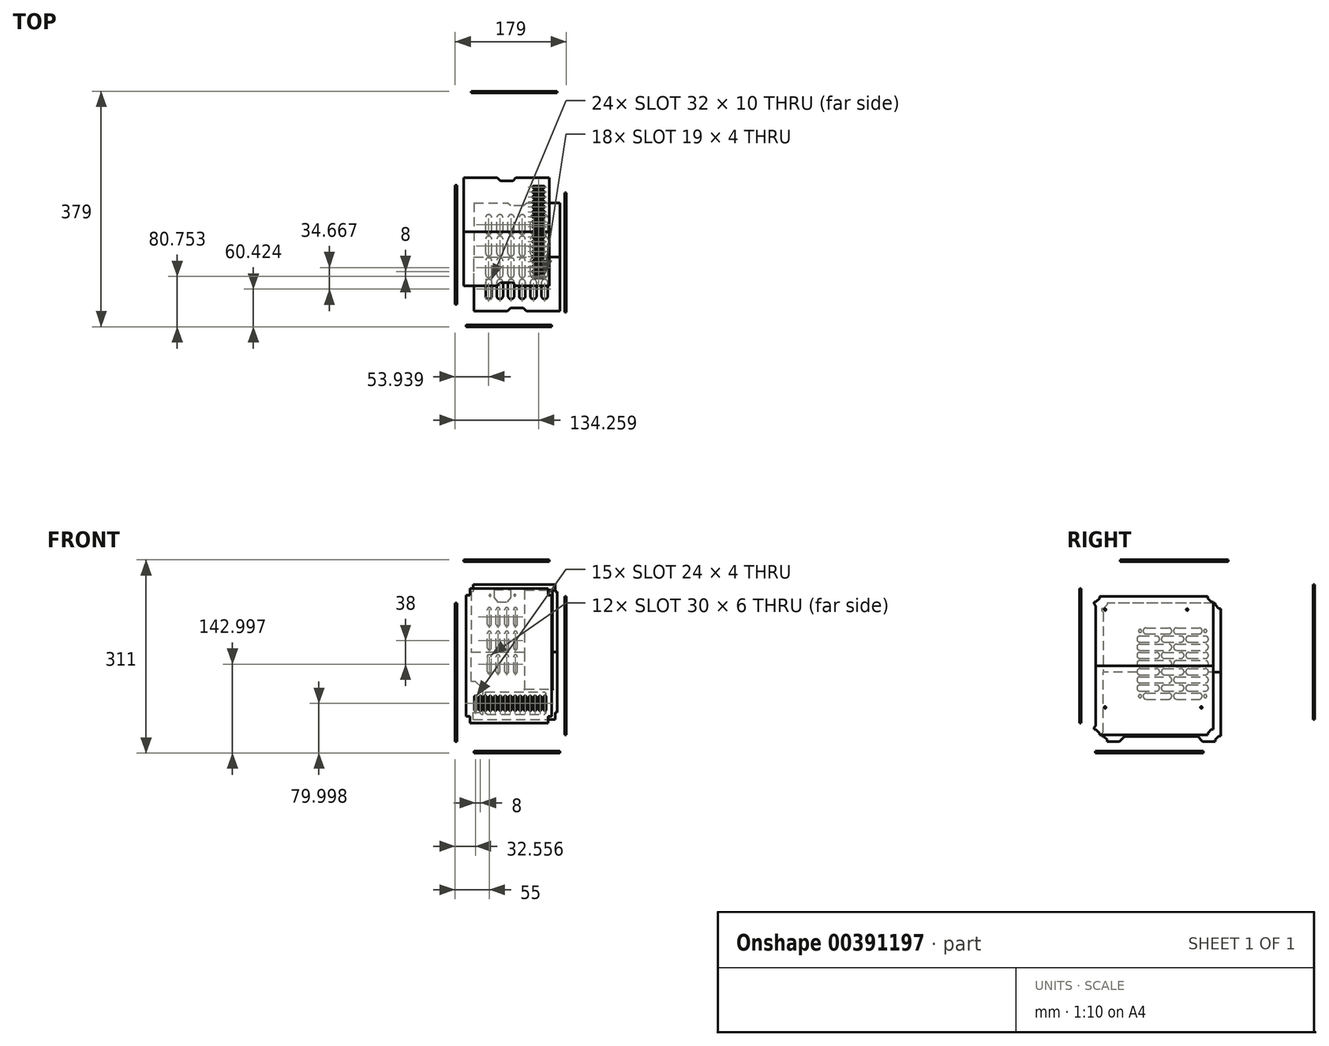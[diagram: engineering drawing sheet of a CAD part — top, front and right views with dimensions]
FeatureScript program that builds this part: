
annotation { "Feature Type Name" : "Feature", "Feature Type Description" : "" }
export const myFeature = defineFeature(function(context is Context, id is Id, definition is map)
    precondition{}
    {
        {
            var Q0;
            Q0=qCreatedBy(makeId("Front.planeOp"),FACE);
            var sketch = newSketch(context, id + "F0", { "sketchPlane" : qUnion([Q0])});
            skLineSegment(sketch, "E0.bottom", {"start": v(-78.44, 112) * mm, "end": v(59.56, 112) * mm});
            skLineSegment(sketch, "E0.top", {"start": v(-78.44, 3.5) * mm, "end": v(59.56, 3.5) * mm});
            skLineSegment(sketch, "E0.left", {"start": v(-78.44, 112) * mm, "end": v(-78.44, 3.5) * mm});
            skLineSegment(sketch, "E0.right", {"start": v(59.56, 112) * mm, "end": v(59.56, 3.5) * mm});
            skLineSegment(sketch, "E1", {"start": v(-78.44, 100.9) * mm, "end": v(-72.34, 100.9) * mm});
            skLineSegment(sketch, "E2", {"start": v(-72.34, 100.9) * mm, "end": v(-72.34, 112) * mm});
            skLineSegment(sketch, "E3", {"start": v(53.46, 112) * mm, "end": v(53.46, 100.9) * mm});
            skLineSegment(sketch, "E4", {"start": v(53.46, 100.9) * mm, "end": v(59.56, 100.9) * mm});
            skSolve(sketch);
        }
        {
            var Q0;
            {var subQ1=sQuery(id+"F0.wireOp",EDGE,"E0.top");Q0=makeQuery(id+"F0.imprint","IMPRINT",FACE,{"disambiguationData":[TD([[makeQuery(id+"F0.imprint","IMPRINT",EDGE,{"derivedFrom":subQ1}),1.0]])]});}
            extrude(context, id + "F1", {"entities" : qUnion([Q0]), "depth" : 3 * mm});
        }
        {
            var Q0;
            Q0=makeQuery(id+"F1.opExtrude","SWEPT_BODY",BODY,{"disambiguationData":[OSD([sQuery(id+"F0.wireOp",EDGE,"E0.bottom"),sQuery(id+"F0.wireOp",EDGE,"E0.top"),sQuery(id+"F0.wireOp",EDGE,"E0.left"),sQuery(id+"F0.wireOp",EDGE,"E0.right"),sQuery(id+"F0.wireOp",EDGE,"f4ycc0LQ-zHDD-6vh2-nqyr-j4wCRgx8H2At"),sQuery(id+"F0.wireOp",EDGE,"8WAKjnjZ-eP6i-UWzr-gM63-qz3cF0Hyub4H"),sQuery(id+"F0.wireOp",EDGE,"8kIEKiAh-QTEb-dtpp-JcTS-wpPMPQfBbqQd"),sQuery(id+"F0.wireOp",EDGE,"IAD0FTGy-GJaP-wMLm-guci-XfnhwucHu2uu"),sQuery(id+"F0.wireOp",EDGE,"IvHsRxJE-VIxi-RXbs-pRJC-tqeUj7lQNFDg"),sQuery(id+"F0.wireOp",EDGE,"jDx6nEBO-jJHg-Gf5S-wIms-nsZNRVFYcTxt")])]});
            var Q1;
            Q1=makeQuery(id+"F1.opExtrude","SWEPT_FACE",FACE,{"disambiguationData":[OSD([sQuery(id+"F0.wireOp",EDGE,"E0.top")])]});
            mirror(context, id + "F2", {"operationType" : NewBodyOperationType.ADD, "entities" : qUnion([Q0]), "mirrorPlane" : qUnion([Q1])});
        }
        {
            var Q0;
            {var subQ0=makeQuery(id+"F1.opExtrude","CAP_FACE",FACE,{"disambiguationData":[OSD([sQuery(id+"F0.wireOp",EDGE,"E0.bottom"),sQuery(id+"F0.wireOp",EDGE,"E0.top"),sQuery(id+"F0.wireOp",EDGE,"E0.left"),sQuery(id+"F0.wireOp",EDGE,"E0.right"),sQuery(id+"F0.wireOp",EDGE,"f4ycc0LQ-zHDD-6vh2-nqyr-j4wCRgx8H2At"),sQuery(id+"F0.wireOp",EDGE,"8WAKjnjZ-eP6i-UWzr-gM63-qz3cF0Hyub4H"),sQuery(id+"F0.wireOp",EDGE,"8kIEKiAh-QTEb-dtpp-JcTS-wpPMPQfBbqQd"),sQuery(id+"F0.wireOp",EDGE,"IAD0FTGy-GJaP-wMLm-guci-XfnhwucHu2uu"),sQuery(id+"F0.wireOp",EDGE,"IvHsRxJE-VIxi-RXbs-pRJC-tqeUj7lQNFDg"),sQuery(id+"F0.wireOp",EDGE,"jDx6nEBO-jJHg-Gf5S-wIms-nsZNRVFYcTxt")])],"isStart":false});Q0=makeQuery(id+"F2.boolean.opBoolean","MERGE",FACE,{"derivedFrom":[subQ0,makeQuery(id+"F2.opPattern","COPY",FACE,{"derivedFrom":subQ0,"instanceName":"1"})]});}
            var sketch = newSketch(context, id + "F3", { "sketchPlane" : qUnion([Q0])});
            skLineSegment(sketch, "E5", {"start": v(-78.44, -63) * mm, "end": v(-63.44, -63) * mm, "construction": true});
            skLineSegment(sketch, "E6", {"start": v(-63.44, -63) * mm, "end": v(-63.44, -83) * mm, "construction": true});
            skArc(sketch, "E7.0.startCap", {"start": v(-65.44, -63) * mm, "mid": v(-63.44, -61) * mm, "end": v(-61.44, -63) * mm});
            skArc(sketch, "E7.0.endCap", {"start": v(-61.44, -83) * mm, "mid": v(-63.44, -85) * mm, "end": v(-65.44, -83) * mm});
            skLineSegment(sketch, "E7.0.left", {"start": v(-61.44, -63) * mm, "end": v(-61.44, -83) * mm});
            skLineSegment(sketch, "E7.0.right", {"start": v(-65.44, -63) * mm, "end": v(-65.44, -83) * mm});
            skLineSegment(sketch, "E8.1.0.0", {"start": v(-55.44, -63) * mm, "end": v(-55.44, -83) * mm, "construction": true});
            skArc(sketch, "E8.1.0.1", {"start": v(-57.44, -63) * mm, "mid": v(-55.44, -61) * mm, "end": v(-53.44, -63) * mm});
            skArc(sketch, "E8.1.0.2", {"start": v(-53.44, -83) * mm, "mid": v(-55.44, -85) * mm, "end": v(-57.44, -83) * mm});
            skLineSegment(sketch, "E8.1.0.3", {"start": v(-53.44, -63) * mm, "end": v(-53.44, -83) * mm});
            skLineSegment(sketch, "E8.1.0.4", {"start": v(-57.44, -63) * mm, "end": v(-57.44, -83) * mm});
            skLineSegment(sketch, "E8.2.0.0", {"start": v(-47.44, -63) * mm, "end": v(-47.44, -83) * mm, "construction": true});
            skArc(sketch, "E8.2.0.1", {"start": v(-49.44, -63) * mm, "mid": v(-47.44, -61) * mm, "end": v(-45.44, -63) * mm});
            skArc(sketch, "E8.2.0.2", {"start": v(-45.44, -83) * mm, "mid": v(-47.44, -85) * mm, "end": v(-49.44, -83) * mm});
            skLineSegment(sketch, "E8.2.0.3", {"start": v(-45.44, -63) * mm, "end": v(-45.44, -83) * mm});
            skLineSegment(sketch, "E8.2.0.4", {"start": v(-49.44, -63) * mm, "end": v(-49.44, -83) * mm});
            skLineSegment(sketch, "E8.3.0.0", {"start": v(-39.44, -63) * mm, "end": v(-39.44, -83) * mm, "construction": true});
            skArc(sketch, "E8.3.0.1", {"start": v(-41.44, -63) * mm, "mid": v(-39.44, -61) * mm, "end": v(-37.44, -63) * mm});
            skArc(sketch, "E8.3.0.2", {"start": v(-37.44, -83) * mm, "mid": v(-39.44, -85) * mm, "end": v(-41.44, -83) * mm});
            skLineSegment(sketch, "E8.3.0.3", {"start": v(-37.44, -63) * mm, "end": v(-37.44, -83) * mm});
            skLineSegment(sketch, "E8.3.0.4", {"start": v(-41.44, -63) * mm, "end": v(-41.44, -83) * mm});
            skLineSegment(sketch, "E8.4.0.0", {"start": v(-31.44, -63) * mm, "end": v(-31.44, -83) * mm, "construction": true});
            skArc(sketch, "E8.4.0.1", {"start": v(-33.44, -63) * mm, "mid": v(-31.44, -61) * mm, "end": v(-29.44, -63) * mm});
            skArc(sketch, "E8.4.0.2", {"start": v(-29.44, -83) * mm, "mid": v(-31.44, -85) * mm, "end": v(-33.44, -83) * mm});
            skLineSegment(sketch, "E8.4.0.3", {"start": v(-29.44, -63) * mm, "end": v(-29.44, -83) * mm});
            skLineSegment(sketch, "E8.4.0.4", {"start": v(-33.44, -63) * mm, "end": v(-33.44, -83) * mm});
            skLineSegment(sketch, "E8.5.0.0", {"start": v(-23.44, -63) * mm, "end": v(-23.44, -83) * mm, "construction": true});
            skArc(sketch, "E8.5.0.1", {"start": v(-25.44, -63) * mm, "mid": v(-23.44, -61) * mm, "end": v(-21.44, -63) * mm});
            skArc(sketch, "E8.5.0.2", {"start": v(-21.44, -83) * mm, "mid": v(-23.44, -85) * mm, "end": v(-25.44, -83) * mm});
            skLineSegment(sketch, "E8.5.0.3", {"start": v(-21.44, -63) * mm, "end": v(-21.44, -83) * mm});
            skLineSegment(sketch, "E8.5.0.4", {"start": v(-25.44, -63) * mm, "end": v(-25.44, -83) * mm});
            skLineSegment(sketch, "E8.6.0.0", {"start": v(-15.44, -63) * mm, "end": v(-15.44, -83) * mm, "construction": true});
            skArc(sketch, "E8.6.0.1", {"start": v(-17.44, -63) * mm, "mid": v(-15.44, -61) * mm, "end": v(-13.44, -63) * mm});
            skArc(sketch, "E8.6.0.2", {"start": v(-13.44, -83) * mm, "mid": v(-15.44, -85) * mm, "end": v(-17.44, -83) * mm});
            skLineSegment(sketch, "E8.6.0.3", {"start": v(-13.44, -63) * mm, "end": v(-13.44, -83) * mm});
            skLineSegment(sketch, "E8.6.0.4", {"start": v(-17.44, -63) * mm, "end": v(-17.44, -83) * mm});
            skLineSegment(sketch, "E8.7.0.0", {"start": v(-7.44, -63) * mm, "end": v(-7.44, -83) * mm, "construction": true});
            skArc(sketch, "E8.7.0.1", {"start": v(-9.44, -63) * mm, "mid": v(-7.44, -61) * mm, "end": v(-5.44, -63) * mm});
            skArc(sketch, "E8.7.0.2", {"start": v(-5.44, -83) * mm, "mid": v(-7.44, -85) * mm, "end": v(-9.44, -83) * mm});
            skLineSegment(sketch, "E8.7.0.3", {"start": v(-5.44, -63) * mm, "end": v(-5.44, -83) * mm});
            skLineSegment(sketch, "E8.7.0.4", {"start": v(-9.44, -63) * mm, "end": v(-9.44, -83) * mm});
            skLineSegment(sketch, "E8.8.0.0", {"start": v(0.56, -63) * mm, "end": v(0.56, -83) * mm, "construction": true});
            skArc(sketch, "E8.8.0.1", {"start": v(-1.44, -63) * mm, "mid": v(0.56, -61) * mm, "end": v(2.56, -63) * mm});
            skArc(sketch, "E8.8.0.2", {"start": v(2.56, -83) * mm, "mid": v(0.56, -85) * mm, "end": v(-1.44, -83) * mm});
            skLineSegment(sketch, "E8.8.0.3", {"start": v(2.56, -63) * mm, "end": v(2.56, -83) * mm});
            skLineSegment(sketch, "E8.8.0.4", {"start": v(-1.44, -63) * mm, "end": v(-1.44, -83) * mm});
            skLineSegment(sketch, "E8.9.0.0", {"start": v(8.56, -63) * mm, "end": v(8.56, -83) * mm, "construction": true});
            skArc(sketch, "E8.9.0.1", {"start": v(6.56, -63) * mm, "mid": v(8.56, -61) * mm, "end": v(10.56, -63) * mm});
            skArc(sketch, "E8.9.0.2", {"start": v(10.56, -83) * mm, "mid": v(8.56, -85) * mm, "end": v(6.56, -83) * mm});
            skLineSegment(sketch, "E8.9.0.3", {"start": v(10.56, -63) * mm, "end": v(10.56, -83) * mm});
            skLineSegment(sketch, "E8.9.0.4", {"start": v(6.56, -63) * mm, "end": v(6.56, -83) * mm});
            skLineSegment(sketch, "E8.10.0.0", {"start": v(16.56, -63) * mm, "end": v(16.56, -83) * mm, "construction": true});
            skArc(sketch, "E8.10.0.1", {"start": v(14.56, -63) * mm, "mid": v(16.56, -61) * mm, "end": v(18.56, -63) * mm});
            skArc(sketch, "E8.10.0.2", {"start": v(18.56, -83) * mm, "mid": v(16.56, -85) * mm, "end": v(14.56, -83) * mm});
            skLineSegment(sketch, "E8.10.0.3", {"start": v(18.56, -63) * mm, "end": v(18.56, -83) * mm});
            skLineSegment(sketch, "E8.10.0.4", {"start": v(14.56, -63) * mm, "end": v(14.56, -83) * mm});
            skLineSegment(sketch, "E8.11.0.0", {"start": v(24.56, -63) * mm, "end": v(24.56, -83) * mm, "construction": true});
            skArc(sketch, "E8.11.0.1", {"start": v(22.56, -63) * mm, "mid": v(24.56, -61) * mm, "end": v(26.56, -63) * mm});
            skArc(sketch, "E8.11.0.2", {"start": v(26.56, -83) * mm, "mid": v(24.56, -85) * mm, "end": v(22.56, -83) * mm});
            skLineSegment(sketch, "E8.11.0.3", {"start": v(26.56, -63) * mm, "end": v(26.56, -83) * mm});
            skLineSegment(sketch, "E8.11.0.4", {"start": v(22.56, -63) * mm, "end": v(22.56, -83) * mm});
            skLineSegment(sketch, "E8.12.0.0", {"start": v(32.56, -63) * mm, "end": v(32.56, -83) * mm, "construction": true});
            skArc(sketch, "E8.12.0.1", {"start": v(30.56, -63) * mm, "mid": v(32.56, -61) * mm, "end": v(34.56, -63) * mm});
            skArc(sketch, "E8.12.0.2", {"start": v(34.56, -83) * mm, "mid": v(32.56, -85) * mm, "end": v(30.56, -83) * mm});
            skLineSegment(sketch, "E8.12.0.3", {"start": v(34.56, -63) * mm, "end": v(34.56, -83) * mm});
            skLineSegment(sketch, "E8.12.0.4", {"start": v(30.56, -63) * mm, "end": v(30.56, -83) * mm});
            skLineSegment(sketch, "E8.13.0.0", {"start": v(40.56, -63) * mm, "end": v(40.56, -83) * mm, "construction": true});
            skArc(sketch, "E8.13.0.1", {"start": v(38.56, -63) * mm, "mid": v(40.56, -61) * mm, "end": v(42.56, -63) * mm});
            skArc(sketch, "E8.13.0.2", {"start": v(42.56, -83) * mm, "mid": v(40.56, -85) * mm, "end": v(38.56, -83) * mm});
            skLineSegment(sketch, "E8.13.0.3", {"start": v(42.56, -63) * mm, "end": v(42.56, -83) * mm});
            skLineSegment(sketch, "E8.13.0.4", {"start": v(38.56, -63) * mm, "end": v(38.56, -83) * mm});
            skLineSegment(sketch, "E8.14.0.0", {"start": v(48.56, -63) * mm, "end": v(48.56, -83) * mm, "construction": true});
            skArc(sketch, "E8.14.0.1", {"start": v(46.56, -63) * mm, "mid": v(48.56, -61) * mm, "end": v(50.56, -63) * mm});
            skArc(sketch, "E8.14.0.2", {"start": v(50.56, -83) * mm, "mid": v(48.56, -85) * mm, "end": v(46.56, -83) * mm});
            skLineSegment(sketch, "E8.14.0.3", {"start": v(50.56, -63) * mm, "end": v(50.56, -83) * mm});
            skLineSegment(sketch, "E8.14.0.4", {"start": v(46.56, -63) * mm, "end": v(46.56, -83) * mm});
            skLineSegment(sketch, "E8.direction1", {"start": v(-65.44, -83) * mm, "end": v(-57.44, -83) * mm, "construction": true});
            skSolve(sketch);
        }
        {
            var Q0;
            Q0=qSketchRegion(id+"F3",true);
            extrude(context, id + "F4", {"entities" : qUnion([Q0]), "operationType" : NewBodyOperationType.REMOVE, "oppositeDirection" : true, "depth" : 3 * mm});
        }
        {
            var Q0;
            Q0=qCreatedBy(makeId("Right.planeOp"),FACE);
            cPlane(context, id + "F5", {"entities" : qUnion([Q0]), "cplaneType" : CPlaneType.OFFSET, "offset" : 80 * mm, "width" : 150 * mm, "height" : 150 * mm});
        }
        {
            var Q0;
            Q0=qCreatedBy(id+"F5.planeOp",FACE);
            var sketch = newSketch(context, id + "F6", { "sketchPlane" : qUnion([Q0])});
            skLineSegment(sketch, "E9.bottom", {"start": v(20.48, 98.93) * mm, "end": v(212.48, 98.93) * mm});
            skLineSegment(sketch, "E9.top", {"start": v(20.48, -12.57) * mm, "end": v(212.48, -12.57) * mm});
            skLineSegment(sketch, "E9.left", {"start": v(20.48, 98.93) * mm, "end": v(20.48, -12.57) * mm});
            skLineSegment(sketch, "E9.right", {"start": v(212.48, 98.93) * mm, "end": v(212.48, -12.57) * mm});
            skLineSegment(sketch, "E10", {"start": v(20.48, 89.93) * mm, "end": v(23.48, 89.93) * mm});
            skLineSegment(sketch, "E11", {"start": v(23.48, 89.93) * mm, "end": v(29.48, 95.93) * mm});
            skLineSegment(sketch, "E12", {"start": v(29.48, 95.93) * mm, "end": v(29.48, 98.93) * mm});
            skLineSegment(sketch, "E13", {"start": v(20.48, 86.93) * mm, "end": v(23.48, 83.93) * mm});
            skLineSegment(sketch, "E14", {"start": v(23.48, 83.93) * mm, "end": v(23.48, -12.57) * mm});
            skLineSegment(sketch, "E15", {"start": v(203.48, 98.93) * mm, "end": v(203.48, 95.93) * mm});
            skLineSegment(sketch, "E16", {"start": v(203.48, 95.93) * mm, "end": v(209.48, 89.93) * mm});
            skLineSegment(sketch, "E17", {"start": v(209.48, 89.93) * mm, "end": v(212.48, 89.93) * mm});
            skLineSegment(sketch, "E18", {"start": v(212.48, 86.93) * mm, "end": v(209.48, 83.93) * mm});
            skLineSegment(sketch, "E19", {"start": v(209.48, 83.93) * mm, "end": v(209.48, -12.57) * mm});
            skSolve(sketch);
        }
        {
            var Q0;
            {var subQ3=sQuery(id+"F6.wireOp",EDGE,"E10");Q0=makeQuery(id+"F6.imprint","IMPRINT",FACE,{"disambiguationData":[TD([[makeQuery(id+"F6.imprint","IMPRINT",EDGE,{"derivedFrom":subQ3}),-1.0]])]});}
            var Q1;
            {var subQ4=sQuery(id+"F6.wireOp",EDGE,"E18");Q1=makeQuery(id+"F6.imprint","IMPRINT",FACE,{"disambiguationData":[TD([[makeQuery(id+"F6.imprint","IMPRINT",EDGE,{"derivedFrom":subQ4}),1.0]])]});}
            extrude(context, id + "F7", {"entities" : qUnion([Q0, Q1]), "depth" : 3 * mm});
        }
        {
            var Q0;
            Q0=makeQuery(id+"F7.opExtrude","SWEPT_BODY",BODY,{"disambiguationData":[OSD([sQuery(id+"F6.wireOp",EDGE,"E9.bottom"),sQuery(id+"F6.wireOp",EDGE,"E9.top"),sQuery(id+"F6.wireOp",EDGE,"E9.left"),sQuery(id+"F6.wireOp",EDGE,"E9.right"),sQuery(id+"F6.wireOp",EDGE,"uhohLnhp-hqEh-HnCf-sw5P-UAyFwgDYjcBT"),sQuery(id+"F6.wireOp",EDGE,"PZ9vbapj-Vyhe-IVd5-wSIB-ihSb0FTefDFo"),sQuery(id+"F6.wireOp",EDGE,"Vy2RlQAS-aQ6k-OJzX-lqoE-WAFZ4NoHzz8E"),sQuery(id+"F6.wireOp",EDGE,"uOpGianr-bHoC-LPpd-ZrnQ-WT6fRq75YZDk"),sQuery(id+"F6.wireOp",EDGE,"ByD4MoDk-9vtG-w2Bj-nV2I-deXss6nWGu8L"),sQuery(id+"F6.wireOp",EDGE,"dErzSW6J-HGX5-GNXE-lozc-OmhnMsFbACEc"),sQuery(id+"F6.wireOp",EDGE,"oiYVu7ST-duG0-g5FE-uATR-zlAqLM0uh895"),sQuery(id+"F6.wireOp",EDGE,"fhnCciFL-T4Vn-rBCZ-nkKt-uSig2OXv9zq8")])]});
            var Q1;
            Q1=makeQuery(id+"F7.opExtrude","SWEPT_FACE",FACE,{"disambiguationData":[OSD([sQuery(id+"F6.wireOp",EDGE,"E9.top")])]});
            mirror(context, id + "F8", {"operationType" : NewBodyOperationType.ADD, "entities" : qUnion([Q0]), "mirrorPlane" : qUnion([Q1])});
        }
        {
            var Q0;
            {var subQ0=makeQuery(id+"F7.opExtrude","CAP_FACE",FACE,{"disambiguationData":[OSD([sQuery(id+"F6.wireOp",EDGE,"E9.bottom"),sQuery(id+"F6.wireOp",EDGE,"E9.top"),sQuery(id+"F6.wireOp",EDGE,"E9.left"),sQuery(id+"F6.wireOp",EDGE,"E9.right"),sQuery(id+"F6.wireOp",EDGE,"E10"),sQuery(id+"F6.wireOp",EDGE,"E11"),sQuery(id+"F6.wireOp",EDGE,"E12"),sQuery(id+"F6.wireOp",EDGE,"E13"),sQuery(id+"F6.wireOp",EDGE,"E14"),sQuery(id+"F6.wireOp",EDGE,"E15"),sQuery(id+"F6.wireOp",EDGE,"E16"),sQuery(id+"F6.wireOp",EDGE,"E17")])],"isStart":false});Q0=makeQuery(id+"F8.boolean.opBoolean","MERGE",FACE,{"derivedFrom":[subQ0,makeQuery(id+"F8.opPattern","COPY",FACE,{"derivedFrom":subQ0,"instanceName":"1"})]});}
            var sketch = newSketch(context, id + "F9", { "sketchPlane" : qUnion([Q0])});
            skLineSegment(sketch, "E20", {"start": v(212.48, -115.07) * mm, "end": v(212.48, -124.07) * mm, "construction": true});
            skLineSegment(sketch, "E21", {"start": v(212.48, -124.07) * mm, "end": v(203.48, -124.07) * mm, "construction": true});
            skLineSegment(sketch, "E22", {"start": v(203.48, -124.07) * mm, "end": v(203.48, -86.07) * mm, "construction": true});
            skLineSegment(sketch, "E23", {"start": v(203.48, -86.07) * mm, "end": v(203.48, 83.93) * mm, "construction": true});
            skLineSegment(sketch, "E24", {"start": v(203.48, 83.93) * mm, "end": v(33.48, 83.93) * mm, "construction": true});
            skLineSegment(sketch, "E25", {"start": v(33.48, 83.93) * mm, "end": v(33.48, -86.07) * mm, "construction": true});
            skLineSegment(sketch, "E26", {"start": v(33.48, -86.07) * mm, "end": v(203.48, -86.07) * mm, "construction": true});
            skLineSegment(sketch, "E27", {"start": v(33.48, -79.67) * mm, "end": v(38.38, -79.67) * mm, "construction": true});
            skCircle(sketch, "E28", {"center": v(38.38, -79.67) * mm, "radius": 1.5 * mm});
            skLineSegment(sketch, "E29", {"start": v(33.48, 77.73) * mm, "end": v(38.38, 77.73) * mm, "construction": true});
            skCircle(sketch, "E30", {"center": v(38.38, 77.73) * mm, "radius": 1.5 * mm});
            skLineSegment(sketch, "E31", {"start": v(203.48, 77.73) * mm, "end": v(170.48, 77.73) * mm, "construction": true});
            skCircle(sketch, "E32", {"center": v(170.48, 77.73) * mm, "radius": 1.5 * mm});
            skLineSegment(sketch, "E33", {"start": v(203.48, -79.67) * mm, "end": v(193.28, -79.67) * mm, "construction": true});
            skCircle(sketch, "E34", {"center": v(193.28, -79.67) * mm, "radius": 1.5 * mm});
            skSolve(sketch);
        }
        {
            var Q0;
            Q0 = qSketchRegion(id + "F9", true);
            extrude(context, id + "F10", {"entities" : qUnion([Q0]), "operationType" : NewBodyOperationType.REMOVE, "oppositeDirection" : true, "depth" : 25 * mm});
        }
        {
            var Q0;
            Q0=qCreatedBy(makeId("Right.planeOp"),FACE);
            cPlane(context, id + "F11", {"entities" : qUnion([Q0]), "cplaneType" : CPlaneType.OFFSET, "offset" : 96 * mm, "oppositeDirection" : true, "width" : 150 * mm, "height" : 150 * mm});
        }
        {
            var Q0;
            Q0=qCreatedBy(id+"F11.planeOp",FACE);
            var sketch = newSketch(context, id + "F12", { "sketchPlane" : qUnion([Q0])});
            skLineSegment(sketch, "E35.bottom", {"start": v(224.63, 88.49) * mm, "end": v(32.63, 88.49) * mm});
            skLineSegment(sketch, "E35.top", {"start": v(224.63, -23.01) * mm, "end": v(32.63, -23.01) * mm});
            skLineSegment(sketch, "E35.left", {"start": v(224.63, 88.49) * mm, "end": v(224.63, -23.01) * mm});
            skLineSegment(sketch, "E35.right", {"start": v(32.63, 88.49) * mm, "end": v(32.63, -23.01) * mm});
            skLineSegment(sketch, "E36", {"start": v(215.63, 88.49) * mm, "end": v(215.63, 85.49) * mm});
            skLineSegment(sketch, "E37", {"start": v(215.63, 85.49) * mm, "end": v(221.63, 79.49) * mm});
            skLineSegment(sketch, "E38", {"start": v(221.63, 79.49) * mm, "end": v(224.63, 79.49) * mm});
            skLineSegment(sketch, "E39", {"start": v(41.63, 88.49) * mm, "end": v(41.63, 85.49) * mm});
            skLineSegment(sketch, "E40", {"start": v(41.63, 85.49) * mm, "end": v(35.63, 79.49) * mm});
            skLineSegment(sketch, "E41", {"start": v(35.63, 79.49) * mm, "end": v(32.63, 79.49) * mm});
            skLineSegment(sketch, "E42", {"start": v(32.63, 76.49) * mm, "end": v(35.63, 73.49) * mm});
            skLineSegment(sketch, "E43", {"start": v(35.63, 73.49) * mm, "end": v(35.63, -23.01) * mm});
            skSolve(sketch);
        }
        {
            var Q0;
            {var subQ2=sQuery(id+"F12.wireOp",EDGE,"E36");Q0=makeQuery(id+"F12.imprint","IMPRINT",FACE,{"disambiguationData":[TD([[makeQuery(id+"F12.imprint","IMPRINT",EDGE,{"derivedFrom":subQ2}),-1.0]])]});}
            extrude(context, id + "F13", {"entities" : qUnion([Q0]), "depth" : 3 * mm});
        }
        {
            var Q0;
            Q0=makeQuery(id+"F13.opExtrude","SWEPT_BODY",BODY,{"disambiguationData":[OSD([sQuery(id+"F12.wireOp",EDGE,"E35.bottom"),sQuery(id+"F12.wireOp",EDGE,"E35.top"),sQuery(id+"F12.wireOp",EDGE,"E35.left"),sQuery(id+"F12.wireOp",EDGE,"E35.right"),sQuery(id+"F12.wireOp",EDGE,"RUecidL0-44Lw-8r9P-yNFq-6MCyUiE8M5dH"),sQuery(id+"F12.wireOp",EDGE,"1PHfe21F-eU2c-dzBH-LU7s-Lgz8jYdCAyph")])]});
            var Q1;
            Q1=makeQuery(id+"F13.opExtrude","SWEPT_FACE",FACE,{"disambiguationData":[OSD([sQuery(id+"F12.wireOp",EDGE,"E35.top")])]});
            mirror(context, id + "F14", {"operationType" : NewBodyOperationType.ADD, "entities" : qUnion([Q0]), "mirrorPlane" : qUnion([Q1])});
        }
        {
            var Q0;
            {var subQ0=makeQuery(id+"F13.opExtrude","CAP_FACE",FACE,{"disambiguationData":[OSD([sQuery(id+"F12.wireOp",EDGE,"E35.bottom"),sQuery(id+"F12.wireOp",EDGE,"E35.top"),sQuery(id+"F12.wireOp",EDGE,"E35.left"),sQuery(id+"F12.wireOp",EDGE,"E35.right"),sQuery(id+"F12.wireOp",EDGE,"RUecidL0-44Lw-8r9P-yNFq-6MCyUiE8M5dH"),sQuery(id+"F12.wireOp",EDGE,"1PHfe21F-eU2c-dzBH-LU7s-Lgz8jYdCAyph")])],"isStart":true});Q0=makeQuery(id+"F14.boolean.opBoolean","MERGE",FACE,{"derivedFrom":[subQ0,makeQuery(id+"F14.opPattern","COPY",FACE,{"derivedFrom":subQ0,"instanceName":"1"})]});}
            var sketch = newSketch(context, id + "F15", { "sketchPlane" : qUnion([Q0])});
            skLineSegment(sketch, "E44", {"start": v(-224.63, 48.49) * mm, "end": v(-199.63, 48.49) * mm, "construction": true});
            skLineSegment(sketch, "E45", {"start": v(-199.63, 48.49) * mm, "end": v(-199.63, -66.51) * mm, "construction": true});
            skLineSegment(sketch, "E46", {"start": v(-199.63, 43.49) * mm, "end": v(-189.63, 43.49) * mm, "construction": true});
            skLineSegment(sketch, "E47", {"start": v(-189.63, 43.49) * mm, "end": v(-153.63, 43.49) * mm, "construction": true});
            skLineSegment(sketch, "E48", {"start": v(-199.63, 30.36) * mm, "end": v(-173.3, 30.36) * mm, "construction": true});
            skLineSegment(sketch, "E49", {"start": v(-199.63, 17.24) * mm, "end": v(-153.63, 17.24) * mm, "construction": true});
            skLineSegment(sketch, "E50", {"start": v(-199.63, 4.11) * mm, "end": v(-173.3, 4.11) * mm, "construction": true});
            skLineSegment(sketch, "E51", {"start": v(-199.63, -9.01) * mm, "end": v(-153.63, -9.01) * mm, "construction": true});
            skLineSegment(sketch, "E52", {"start": v(-199.63, -22.14) * mm, "end": v(-173.3, -22.14) * mm, "construction": true});
            skLineSegment(sketch, "E53", {"start": v(-199.63, -35.26) * mm, "end": v(-153.63, -35.26) * mm, "construction": true});
            skLineSegment(sketch, "E54", {"start": v(-199.63, -48.39) * mm, "end": v(-173.3, -48.39) * mm, "construction": true});
            skLineSegment(sketch, "E55", {"start": v(-199.63, -61.51) * mm, "end": v(-189.63, -61.51) * mm, "construction": true});
            skLineSegment(sketch, "E56", {"start": v(-189.63, -61.51) * mm, "end": v(-153.63, -61.51) * mm, "construction": true});
            skCircle(sketch, "E57", {"center": v(-199.63, 43.49) * mm, "radius": 2.5 * mm});
            skLineSegment(sketch, "E58", {"start": v(-104.63, 43.49) * mm, "end": v(-94.63, 43.49) * mm, "construction": true});
            skPoint(sketch, "E58.endSnap0", {"position": v(-94.54, 43.49) * mm});
            skCircle(sketch, "E59", {"center": v(-94.63, 43.49) * mm, "radius": 2.5 * mm});
            skLineSegment(sketch, "E60", {"start": v(-153.63, 43.49) * mm, "end": v(-140.63, 43.49) * mm, "construction": true});
            skLineSegment(sketch, "E61", {"start": v(-140.63, 43.49) * mm, "end": v(-104.63, 43.49) * mm, "construction": true});
            skArc(sketch, "E62.0.startCap", {"start": v(-189.63, 38.49) * mm, "mid": v(-194.63, 43.49) * mm, "end": v(-189.63, 48.49) * mm});
            skArc(sketch, "E62.0.endCap", {"start": v(-153.63, 48.49) * mm, "mid": v(-148.63, 43.49) * mm, "end": v(-153.63, 38.49) * mm});
            skLineSegment(sketch, "E62.0.left", {"start": v(-189.63, 48.49) * mm, "end": v(-153.63, 48.49) * mm});
            skLineSegment(sketch, "E62.0.right", {"start": v(-189.63, 38.49) * mm, "end": v(-153.63, 38.49) * mm});
            skArc(sketch, "E62.1.startCap", {"start": v(-140.63, 38.49) * mm, "mid": v(-145.63, 43.49) * mm, "end": v(-140.63, 48.49) * mm});
            skArc(sketch, "E62.1.endCap", {"start": v(-104.63, 48.49) * mm, "mid": v(-99.63, 43.49) * mm, "end": v(-104.63, 38.49) * mm});
            skLineSegment(sketch, "E62.1.left", {"start": v(-140.63, 48.49) * mm, "end": v(-104.63, 48.49) * mm});
            skLineSegment(sketch, "E62.1.right", {"start": v(-140.63, 38.49) * mm, "end": v(-104.63, 38.49) * mm});
            skLineSegment(sketch, "E63", {"start": v(-173.3, 30.36) * mm, "end": v(-160.3, 30.36) * mm, "construction": true});
            skLineSegment(sketch, "E64", {"start": v(-160.3, 30.36) * mm, "end": v(-133.97, 30.36) * mm, "construction": true});
            skLineSegment(sketch, "E65", {"start": v(-133.97, 30.36) * mm, "end": v(-120.97, 30.36) * mm, "construction": true});
            skLineSegment(sketch, "E66", {"start": v(-120.97, 30.36) * mm, "end": v(-94.63, 30.36) * mm, "construction": true});
            skArc(sketch, "E67.0.startCap", {"start": v(-199.63, 25.36) * mm, "mid": v(-204.63, 30.36) * mm, "end": v(-199.63, 35.36) * mm});
            skArc(sketch, "E67.0.endCap", {"start": v(-173.3, 35.36) * mm, "mid": v(-168.3, 30.36) * mm, "end": v(-173.3, 25.36) * mm});
            skLineSegment(sketch, "E67.0.left", {"start": v(-199.63, 35.36) * mm, "end": v(-173.3, 35.36) * mm});
            skLineSegment(sketch, "E67.0.right", {"start": v(-199.63, 25.36) * mm, "end": v(-173.3, 25.36) * mm});
            skArc(sketch, "E67.1.startCap", {"start": v(-160.3, 25.36) * mm, "mid": v(-165.3, 30.36) * mm, "end": v(-160.3, 35.36) * mm});
            skArc(sketch, "E67.1.endCap", {"start": v(-133.97, 35.36) * mm, "mid": v(-128.97, 30.36) * mm, "end": v(-133.97, 25.36) * mm});
            skLineSegment(sketch, "E67.1.left", {"start": v(-160.3, 35.36) * mm, "end": v(-133.97, 35.36) * mm});
            skLineSegment(sketch, "E67.1.right", {"start": v(-160.3, 25.36) * mm, "end": v(-133.97, 25.36) * mm});
            skArc(sketch, "E67.2.startCap", {"start": v(-120.97, 25.36) * mm, "mid": v(-125.97, 30.36) * mm, "end": v(-120.97, 35.36) * mm});
            skArc(sketch, "E67.2.endCap", {"start": v(-94.63, 35.36) * mm, "mid": v(-89.63, 30.36) * mm, "end": v(-94.63, 25.36) * mm});
            skLineSegment(sketch, "E67.2.left", {"start": v(-120.97, 35.36) * mm, "end": v(-94.63, 35.36) * mm});
            skLineSegment(sketch, "E67.2.right", {"start": v(-120.97, 25.36) * mm, "end": v(-94.63, 25.36) * mm});
            skLineSegment(sketch, "E68", {"start": v(-153.63, 17.24) * mm, "end": v(-140.63, 17.24) * mm, "construction": true});
            skLineSegment(sketch, "E69", {"start": v(-140.63, 17.24) * mm, "end": v(-94.63, 17.24) * mm, "construction": true});
            skArc(sketch, "E70.0.startCap", {"start": v(-199.63, 12.24) * mm, "mid": v(-204.63, 17.24) * mm, "end": v(-199.63, 22.24) * mm});
            skArc(sketch, "E70.0.endCap", {"start": v(-153.63, 22.24) * mm, "mid": v(-148.63, 17.24) * mm, "end": v(-153.63, 12.24) * mm});
            skLineSegment(sketch, "E70.0.left", {"start": v(-199.63, 22.24) * mm, "end": v(-153.63, 22.24) * mm});
            skLineSegment(sketch, "E70.0.right", {"start": v(-199.63, 12.24) * mm, "end": v(-153.63, 12.24) * mm});
            skArc(sketch, "E70.1.startCap", {"start": v(-140.63, 12.24) * mm, "mid": v(-145.63, 17.24) * mm, "end": v(-140.63, 22.24) * mm});
            skArc(sketch, "E70.1.endCap", {"start": v(-94.63, 22.24) * mm, "mid": v(-89.63, 17.24) * mm, "end": v(-94.63, 12.24) * mm});
            skLineSegment(sketch, "E70.1.left", {"start": v(-140.63, 22.24) * mm, "end": v(-94.63, 22.24) * mm});
            skLineSegment(sketch, "E70.1.right", {"start": v(-140.63, 12.24) * mm, "end": v(-94.63, 12.24) * mm});
            skLineSegment(sketch, "E71", {"start": v(-173.3, 4.11) * mm, "end": v(-160.3, 4.11) * mm, "construction": true});
            skLineSegment(sketch, "E72", {"start": v(-160.3, 4.11) * mm, "end": v(-133.97, 4.11) * mm, "construction": true});
            skLineSegment(sketch, "E73", {"start": v(-133.97, 4.11) * mm, "end": v(-120.97, 4.11) * mm, "construction": true});
            skLineSegment(sketch, "E74", {"start": v(-120.97, 4.11) * mm, "end": v(-94.63, 4.11) * mm, "construction": true});
            skArc(sketch, "E75.0.startCap", {"start": v(-199.63, -0.89) * mm, "mid": v(-204.63, 4.11) * mm, "end": v(-199.63, 9.11) * mm});
            skArc(sketch, "E75.0.endCap", {"start": v(-173.3, 9.11) * mm, "mid": v(-168.3, 4.11) * mm, "end": v(-173.3, -0.89) * mm});
            skLineSegment(sketch, "E75.0.left", {"start": v(-199.63, 9.11) * mm, "end": v(-173.3, 9.11) * mm});
            skLineSegment(sketch, "E75.0.right", {"start": v(-199.63, -0.89) * mm, "end": v(-173.3, -0.89) * mm});
            skArc(sketch, "E75.1.startCap", {"start": v(-160.3, -0.89) * mm, "mid": v(-165.3, 4.11) * mm, "end": v(-160.3, 9.11) * mm});
            skArc(sketch, "E75.1.endCap", {"start": v(-133.97, 9.11) * mm, "mid": v(-128.97, 4.11) * mm, "end": v(-133.97, -0.89) * mm});
            skLineSegment(sketch, "E75.1.left", {"start": v(-160.3, 9.11) * mm, "end": v(-133.97, 9.11) * mm});
            skLineSegment(sketch, "E75.1.right", {"start": v(-160.3, -0.89) * mm, "end": v(-133.97, -0.89) * mm});
            skArc(sketch, "E75.2.startCap", {"start": v(-120.97, -0.89) * mm, "mid": v(-125.97, 4.11) * mm, "end": v(-120.97, 9.11) * mm});
            skArc(sketch, "E75.2.endCap", {"start": v(-94.63, 9.11) * mm, "mid": v(-89.63, 4.11) * mm, "end": v(-94.63, -0.89) * mm});
            skLineSegment(sketch, "E75.2.left", {"start": v(-120.97, 9.11) * mm, "end": v(-94.63, 9.11) * mm});
            skLineSegment(sketch, "E75.2.right", {"start": v(-120.97, -0.89) * mm, "end": v(-94.63, -0.89) * mm});
            skLineSegment(sketch, "E76", {"start": v(-153.63, -9.01) * mm, "end": v(-140.63, -9.01) * mm, "construction": true});
            skLineSegment(sketch, "E77", {"start": v(-140.63, -9.01) * mm, "end": v(-94.63, -9.01) * mm, "construction": true});
            skLineSegment(sketch, "E78", {"start": v(-173.3, -22.14) * mm, "end": v(-160.3, -22.14) * mm, "construction": true});
            skLineSegment(sketch, "E79", {"start": v(-160.3, -22.14) * mm, "end": v(-133.97, -22.14) * mm, "construction": true});
            skLineSegment(sketch, "E80", {"start": v(-133.97, -22.14) * mm, "end": v(-120.97, -22.14) * mm, "construction": true});
            skLineSegment(sketch, "E81", {"start": v(-120.97, -22.14) * mm, "end": v(-94.63, -22.14) * mm, "construction": true});
            skLineSegment(sketch, "E82", {"start": v(-153.63, -35.26) * mm, "end": v(-140.63, -35.26) * mm, "construction": true});
            skLineSegment(sketch, "E83", {"start": v(-140.63, -35.26) * mm, "end": v(-94.63, -35.26) * mm, "construction": true});
            skLineSegment(sketch, "E84", {"start": v(-173.3, -48.39) * mm, "end": v(-160.3, -48.39) * mm, "construction": true});
            skLineSegment(sketch, "E85", {"start": v(-160.3, -48.39) * mm, "end": v(-133.97, -48.39) * mm, "construction": true});
            skLineSegment(sketch, "E86", {"start": v(-133.97, -48.39) * mm, "end": v(-120.97, -48.39) * mm, "construction": true});
            skLineSegment(sketch, "E87", {"start": v(-120.97, -48.39) * mm, "end": v(-94.63, -48.39) * mm, "construction": true});
            skLineSegment(sketch, "E88", {"start": v(-153.63, -61.51) * mm, "end": v(-140.63, -61.51) * mm, "construction": true});
            skLineSegment(sketch, "E89", {"start": v(-140.63, -61.51) * mm, "end": v(-104.63, -61.51) * mm, "construction": true});
            skLineSegment(sketch, "E90", {"start": v(-104.63, -61.51) * mm, "end": v(-94.63, -61.51) * mm, "construction": true});
            skArc(sketch, "E91.0.startCap", {"start": v(-199.63, -14.01) * mm, "mid": v(-204.63, -9.01) * mm, "end": v(-199.63, -4.01) * mm});
            skArc(sketch, "E91.0.endCap", {"start": v(-153.63, -4.01) * mm, "mid": v(-148.63, -9.01) * mm, "end": v(-153.63, -14.01) * mm});
            skLineSegment(sketch, "E91.0.left", {"start": v(-199.63, -4.01) * mm, "end": v(-153.63, -4.01) * mm});
            skLineSegment(sketch, "E91.0.right", {"start": v(-199.63, -14.01) * mm, "end": v(-153.63, -14.01) * mm});
            skArc(sketch, "E91.1.startCap", {"start": v(-140.63, -14.01) * mm, "mid": v(-145.63, -9.01) * mm, "end": v(-140.63, -4.01) * mm});
            skArc(sketch, "E91.1.endCap", {"start": v(-94.63, -4.01) * mm, "mid": v(-89.63, -9.01) * mm, "end": v(-94.63, -14.01) * mm});
            skLineSegment(sketch, "E91.1.left", {"start": v(-140.63, -4.01) * mm, "end": v(-94.63, -4.01) * mm});
            skLineSegment(sketch, "E91.1.right", {"start": v(-140.63, -14.01) * mm, "end": v(-94.63, -14.01) * mm});
            skArc(sketch, "E91.2.startCap", {"start": v(-199.63, -27.14) * mm, "mid": v(-204.63, -22.14) * mm, "end": v(-199.63, -17.14) * mm});
            skArc(sketch, "E91.2.endCap", {"start": v(-173.3, -17.14) * mm, "mid": v(-168.3, -22.14) * mm, "end": v(-173.3, -27.14) * mm});
            skLineSegment(sketch, "E91.2.left", {"start": v(-199.63, -17.14) * mm, "end": v(-173.3, -17.14) * mm});
            skLineSegment(sketch, "E91.2.right", {"start": v(-199.63, -27.14) * mm, "end": v(-173.3, -27.14) * mm});
            skArc(sketch, "E91.3.startCap", {"start": v(-160.3, -27.14) * mm, "mid": v(-165.3, -22.14) * mm, "end": v(-160.3, -17.14) * mm});
            skArc(sketch, "E91.3.endCap", {"start": v(-133.97, -17.14) * mm, "mid": v(-128.97, -22.14) * mm, "end": v(-133.97, -27.14) * mm});
            skLineSegment(sketch, "E91.3.left", {"start": v(-160.3, -17.14) * mm, "end": v(-133.97, -17.14) * mm});
            skLineSegment(sketch, "E91.3.right", {"start": v(-160.3, -27.14) * mm, "end": v(-133.97, -27.14) * mm});
            skArc(sketch, "E91.4.startCap", {"start": v(-120.97, -27.14) * mm, "mid": v(-125.97, -22.14) * mm, "end": v(-120.97, -17.14) * mm});
            skArc(sketch, "E91.4.endCap", {"start": v(-94.63, -17.14) * mm, "mid": v(-89.63, -22.14) * mm, "end": v(-94.63, -27.14) * mm});
            skLineSegment(sketch, "E91.4.left", {"start": v(-120.97, -17.14) * mm, "end": v(-94.63, -17.14) * mm});
            skLineSegment(sketch, "E91.4.right", {"start": v(-120.97, -27.14) * mm, "end": v(-94.63, -27.14) * mm});
            skArc(sketch, "E92.0.startCap", {"start": v(-199.63, -40.26) * mm, "mid": v(-204.63, -35.26) * mm, "end": v(-199.63, -30.26) * mm});
            skArc(sketch, "E92.0.endCap", {"start": v(-153.63, -30.26) * mm, "mid": v(-148.63, -35.26) * mm, "end": v(-153.63, -40.26) * mm});
            skLineSegment(sketch, "E92.0.left", {"start": v(-199.63, -30.26) * mm, "end": v(-153.63, -30.26) * mm});
            skLineSegment(sketch, "E92.0.right", {"start": v(-199.63, -40.26) * mm, "end": v(-153.63, -40.26) * mm});
            skArc(sketch, "E92.1.startCap", {"start": v(-140.63, -40.26) * mm, "mid": v(-145.63, -35.26) * mm, "end": v(-140.63, -30.26) * mm});
            skArc(sketch, "E92.1.endCap", {"start": v(-94.63, -30.26) * mm, "mid": v(-89.63, -35.26) * mm, "end": v(-94.63, -40.26) * mm});
            skLineSegment(sketch, "E92.1.left", {"start": v(-140.63, -30.26) * mm, "end": v(-94.63, -30.26) * mm});
            skLineSegment(sketch, "E92.1.right", {"start": v(-140.63, -40.26) * mm, "end": v(-94.63, -40.26) * mm});
            skArc(sketch, "E92.2.startCap", {"start": v(-199.63, -53.39) * mm, "mid": v(-204.63, -48.39) * mm, "end": v(-199.63, -43.39) * mm});
            skArc(sketch, "E92.2.endCap", {"start": v(-173.3, -43.39) * mm, "mid": v(-168.3, -48.39) * mm, "end": v(-173.3, -53.39) * mm});
            skLineSegment(sketch, "E92.2.left", {"start": v(-199.63, -43.39) * mm, "end": v(-173.3, -43.39) * mm});
            skLineSegment(sketch, "E92.2.right", {"start": v(-199.63, -53.39) * mm, "end": v(-173.3, -53.39) * mm});
            skArc(sketch, "E92.3.startCap", {"start": v(-160.3, -53.39) * mm, "mid": v(-165.3, -48.39) * mm, "end": v(-160.3, -43.39) * mm});
            skArc(sketch, "E92.3.endCap", {"start": v(-133.97, -43.39) * mm, "mid": v(-128.97, -48.39) * mm, "end": v(-133.97, -53.39) * mm});
            skLineSegment(sketch, "E92.3.left", {"start": v(-160.3, -43.39) * mm, "end": v(-133.97, -43.39) * mm});
            skLineSegment(sketch, "E92.3.right", {"start": v(-160.3, -53.39) * mm, "end": v(-133.97, -53.39) * mm});
            skArc(sketch, "E92.4.startCap", {"start": v(-120.97, -53.39) * mm, "mid": v(-125.97, -48.39) * mm, "end": v(-120.97, -43.39) * mm});
            skArc(sketch, "E92.4.endCap", {"start": v(-94.63, -43.39) * mm, "mid": v(-89.63, -48.39) * mm, "end": v(-94.63, -53.39) * mm});
            skLineSegment(sketch, "E92.4.left", {"start": v(-120.97, -43.39) * mm, "end": v(-94.63, -43.39) * mm});
            skLineSegment(sketch, "E92.4.right", {"start": v(-120.97, -53.39) * mm, "end": v(-94.63, -53.39) * mm});
            skArc(sketch, "E92.5.startCap", {"start": v(-189.63, -66.51) * mm, "mid": v(-194.63, -61.51) * mm, "end": v(-189.63, -56.51) * mm});
            skArc(sketch, "E92.5.endCap", {"start": v(-153.63, -56.51) * mm, "mid": v(-148.63, -61.51) * mm, "end": v(-153.63, -66.51) * mm});
            skLineSegment(sketch, "E92.5.left", {"start": v(-189.63, -56.51) * mm, "end": v(-153.63, -56.51) * mm});
            skLineSegment(sketch, "E92.5.right", {"start": v(-189.63, -66.51) * mm, "end": v(-153.63, -66.51) * mm});
            skArc(sketch, "E92.6.startCap", {"start": v(-140.63, -66.51) * mm, "mid": v(-145.63, -61.51) * mm, "end": v(-140.63, -56.51) * mm});
            skArc(sketch, "E92.6.endCap", {"start": v(-104.63, -56.51) * mm, "mid": v(-99.63, -61.51) * mm, "end": v(-104.63, -66.51) * mm});
            skLineSegment(sketch, "E92.6.left", {"start": v(-140.63, -56.51) * mm, "end": v(-104.63, -56.51) * mm});
            skLineSegment(sketch, "E92.6.right", {"start": v(-140.63, -66.51) * mm, "end": v(-104.63, -66.51) * mm});
            skCircle(sketch, "E93", {"center": v(-199.63, -61.51) * mm, "radius": 2.5 * mm});
            skCircle(sketch, "E94", {"center": v(-94.63, -61.51) * mm, "radius": 2.5 * mm});
            skLineSegment(sketch, "E95", {"start": v(-195.63, -134.51) * mm, "end": v(-187.63, -126.51) * mm});
            skLineSegment(sketch, "E96", {"start": v(-187.63, -126.51) * mm, "end": v(-69.63, -126.51) * mm});
            skLineSegment(sketch, "E97", {"start": v(-69.63, -126.51) * mm, "end": v(-61.63, -134.51) * mm});
            skLineSegment(sketch, "E98", {"start": v(-195.63, -134.51) * mm, "end": v(-61.63, -134.51) * mm});
            skSolve(sketch);
        }
        {
            var Q0;
            Q0=qSketchRegion(id+"F15",true);
            var Q1;
            {var subQ0=sQuery(id+"F15.wireOp",EDGE,"eD3hBwOG-1YSv-rIqv-KxOD-YYoGhDVYBiqk");Q1=makeQuery(id+"F15.imprint","IMPRINT",FACE,{"disambiguationData":[TD([[makeQuery(id+"F15.imprint","IMPRINT",EDGE,{"derivedFrom":subQ0}),-1.0]])]});}
            extrude(context, id + "F16", {"entities" : qUnion([Q0, Q1]), "operationType" : NewBodyOperationType.REMOVE, "oppositeDirection" : true, "depth" : 25 * mm});
        }
        {
            var Q0;
            Q0=qCreatedBy(makeId("Top.planeOp"),FACE);
            cPlane(context, id + "F17", {"entities" : qUnion([Q0]), "cplaneType" : CPlaneType.OFFSET, "offset" : 155 * mm, "width" : 150 * mm, "height" : 150 * mm});
        }
        {
            var Q0;
            Q0=qCreatedBy(id+"F17.planeOp",FACE);
            var sketch = newSketch(context, id + "F18", { "sketchPlane" : qUnion([Q0])});
            skLineSegment(sketch, "E99.bottom", {"start": v(-82.24, 149.75) * mm, "end": v(55.76, 149.75) * mm});
            skLineSegment(sketch, "E99.top", {"start": v(-82.24, 62.75) * mm, "end": v(55.76, 62.75) * mm});
            skLineSegment(sketch, "E99.left", {"start": v(-82.24, 149.75) * mm, "end": v(-82.24, 62.75) * mm});
            skLineSegment(sketch, "E99.right", {"start": v(55.76, 149.75) * mm, "end": v(55.76, 62.75) * mm});
            skLineSegment(sketch, "E100", {"start": v(-13.24, 62.75) * mm, "end": v(-13.24, 67.75) * mm, "construction": true});
            skLineSegment(sketch, "E101", {"start": v(-13.24, 67.75) * mm, "end": v(-3.24, 67.75) * mm});
            skLineSegment(sketch, "E102", {"start": v(-3.24, 67.75) * mm, "end": v(1.76, 62.75) * mm});
            skLineSegment(sketch, "E103", {"start": v(-13.24, 67.75) * mm, "end": v(-23.24, 67.75) * mm});
            skLineSegment(sketch, "E104", {"start": v(-23.24, 67.75) * mm, "end": v(-28.24, 62.75) * mm});
            skSolve(sketch);
        }
        {
            var Q0;
            {var subQ1=sQuery(id+"F18.wireOp",EDGE,"E99.bottom");Q0=makeQuery(id+"F18.imprint","IMPRINT",FACE,{"disambiguationData":[TD([[makeQuery(id+"F18.imprint","IMPRINT",EDGE,{"derivedFrom":subQ1}),-1.0]])]});}
            extrude(context, id + "F19", {"entities" : qUnion([Q0]), "depth" : 3 * mm});
        }
        {
            var Q0;
            Q0=makeQuery(id+"F19.opExtrude","SWEPT_BODY",BODY,{"disambiguationData":[OSD([sQuery(id+"F18.wireOp",EDGE,"E99.bottom"),sQuery(id+"F18.wireOp",EDGE,"E99.top"),sQuery(id+"F18.wireOp",EDGE,"E99.left"),sQuery(id+"F18.wireOp",EDGE,"E99.right"),sQuery(id+"F18.wireOp",EDGE,"4fVr5wZB-Gd1x-q5xn-H2uU-eLWPSn34jFpE"),sQuery(id+"F18.wireOp",EDGE,"3zsQ1Kl9-2ynF-8LIN-0dku-r61PIn4XyDqG"),sQuery(id+"F18.wireOp",EDGE,"UXQkqX4z-jOis-0Iwp-P2ix-A9E3pHhtgsOQ"),sQuery(id+"F18.wireOp",EDGE,"3vWWXHrD-USzi-pq0a-DAbT-S4VsDlAi9LDj"),sQuery(id+"F18.wireOp",EDGE,"LeDl9sKz-5wQR-wnus-53VY-3W6SMz2K6K2i"),sQuery(id+"F18.wireOp",EDGE,"1wH7Y6pB-1Br9-c6Mt-ri01-EdgmEcDOcEDC")])]});
            var Q1;
            Q1=makeQuery(id+"F19.opExtrude","SWEPT_FACE",FACE,{"disambiguationData":[OSD([sQuery(id+"F18.wireOp",EDGE,"E99.bottom")])]});
            mirror(context, id + "F20", {"operationType" : NewBodyOperationType.ADD, "entities" : qUnion([Q0]), "mirrorPlane" : qUnion([Q1])});
        }
        {
            var Q0;
            {var subQ0=makeQuery(id+"F19.opExtrude","CAP_FACE",FACE,{"disambiguationData":[OSD([sQuery(id+"F18.wireOp",EDGE,"E99.bottom"),sQuery(id+"F18.wireOp",EDGE,"E99.top"),sQuery(id+"F18.wireOp",EDGE,"E99.left"),sQuery(id+"F18.wireOp",EDGE,"E99.right"),sQuery(id+"F18.wireOp",EDGE,"PmmuqjqP-fakE-rUl7-SfPh-O4iSitPU9Icn"),sQuery(id+"F18.wireOp",EDGE,"Ey54hYX9-Uidp-fYkz-JwUx-OF30ZoxVFsVx"),sQuery(id+"F18.wireOp",EDGE,"Zuea3FDG-psWG-Xv5d-9OWu-NIWtDVeBJ300"),sQuery(id+"F18.wireOp",EDGE,"L7DetxIf-2J7h-IQt7-dtoC-ykCOHUJADywv")])],"isStart":false});Q0=makeQuery(id+"F20.boolean.opBoolean","MERGE",FACE,{"derivedFrom":[subQ0,makeQuery(id+"F20.opPattern","COPY",FACE,{"derivedFrom":subQ0,"instanceName":"1"})]});}
            var sketch = newSketch(context, id + "F21", { "sketchPlane" : qUnion([Q0])});
            skLineSegment(sketch, "E105", {"start": v(30.76, 62.75) * mm, "end": v(30.76, 77.75) * mm, "construction": true});
            skLineSegment(sketch, "E106", {"start": v(30.76, 77.75) * mm, "end": v(45.76, 77.75) * mm, "construction": true});
            skArc(sketch, "E107.0.startCap", {"start": v(30.76, 75.75) * mm, "mid": v(28.76, 77.75) * mm, "end": v(30.76, 79.75) * mm});
            skArc(sketch, "E107.0.endCap", {"start": v(45.76, 79.75) * mm, "mid": v(47.76, 77.75) * mm, "end": v(45.76, 75.75) * mm});
            skLineSegment(sketch, "E107.0.left", {"start": v(30.76, 79.75) * mm, "end": v(45.76, 79.75) * mm});
            skLineSegment(sketch, "E107.0.right", {"start": v(30.76, 75.75) * mm, "end": v(45.76, 75.75) * mm});
            skLineSegment(sketch, "E108.0.1.0", {"start": v(30.76, 85.75) * mm, "end": v(45.76, 85.75) * mm, "construction": true});
            skArc(sketch, "E108.0.1.1", {"start": v(30.76, 83.75) * mm, "mid": v(28.76, 85.75) * mm, "end": v(30.76, 87.75) * mm});
            skArc(sketch, "E108.0.1.2", {"start": v(45.76, 87.75) * mm, "mid": v(47.76, 85.75) * mm, "end": v(45.76, 83.75) * mm});
            skLineSegment(sketch, "E108.0.1.3", {"start": v(30.76, 87.75) * mm, "end": v(45.76, 87.75) * mm});
            skLineSegment(sketch, "E108.0.1.4", {"start": v(30.76, 83.75) * mm, "end": v(45.76, 83.75) * mm});
            skLineSegment(sketch, "E108.0.2.0", {"start": v(30.76, 93.75) * mm, "end": v(45.76, 93.75) * mm, "construction": true});
            skArc(sketch, "E108.0.2.1", {"start": v(30.76, 91.75) * mm, "mid": v(28.76, 93.75) * mm, "end": v(30.76, 95.75) * mm});
            skArc(sketch, "E108.0.2.2", {"start": v(45.76, 95.75) * mm, "mid": v(47.76, 93.75) * mm, "end": v(45.76, 91.75) * mm});
            skLineSegment(sketch, "E108.0.2.3", {"start": v(30.76, 95.75) * mm, "end": v(45.76, 95.75) * mm});
            skLineSegment(sketch, "E108.0.2.4", {"start": v(30.76, 91.75) * mm, "end": v(45.76, 91.75) * mm});
            skLineSegment(sketch, "E108.0.3.0", {"start": v(30.76, 101.75) * mm, "end": v(45.76, 101.75) * mm, "construction": true});
            skArc(sketch, "E108.0.3.1", {"start": v(30.76, 99.75) * mm, "mid": v(28.76, 101.75) * mm, "end": v(30.76, 103.75) * mm});
            skArc(sketch, "E108.0.3.2", {"start": v(45.76, 103.75) * mm, "mid": v(47.76, 101.75) * mm, "end": v(45.76, 99.75) * mm});
            skLineSegment(sketch, "E108.0.3.3", {"start": v(30.76, 103.75) * mm, "end": v(45.76, 103.75) * mm});
            skLineSegment(sketch, "E108.0.3.4", {"start": v(30.76, 99.75) * mm, "end": v(45.76, 99.75) * mm});
            skLineSegment(sketch, "E108.0.4.0", {"start": v(30.76, 109.75) * mm, "end": v(45.76, 109.75) * mm, "construction": true});
            skArc(sketch, "E108.0.4.1", {"start": v(30.76, 107.75) * mm, "mid": v(28.76, 109.75) * mm, "end": v(30.76, 111.75) * mm});
            skArc(sketch, "E108.0.4.2", {"start": v(45.76, 111.75) * mm, "mid": v(47.76, 109.75) * mm, "end": v(45.76, 107.75) * mm});
            skLineSegment(sketch, "E108.0.4.3", {"start": v(30.76, 111.75) * mm, "end": v(45.76, 111.75) * mm});
            skLineSegment(sketch, "E108.0.4.4", {"start": v(30.76, 107.75) * mm, "end": v(45.76, 107.75) * mm});
            skLineSegment(sketch, "E108.0.5.0", {"start": v(30.76, 117.75) * mm, "end": v(45.76, 117.75) * mm, "construction": true});
            skArc(sketch, "E108.0.5.1", {"start": v(30.76, 115.75) * mm, "mid": v(28.76, 117.75) * mm, "end": v(30.76, 119.75) * mm});
            skArc(sketch, "E108.0.5.2", {"start": v(45.76, 119.75) * mm, "mid": v(47.76, 117.75) * mm, "end": v(45.76, 115.75) * mm});
            skLineSegment(sketch, "E108.0.5.3", {"start": v(30.76, 119.75) * mm, "end": v(45.76, 119.75) * mm});
            skLineSegment(sketch, "E108.0.5.4", {"start": v(30.76, 115.75) * mm, "end": v(45.76, 115.75) * mm});
            skLineSegment(sketch, "E108.0.6.0", {"start": v(30.76, 125.75) * mm, "end": v(45.76, 125.75) * mm, "construction": true});
            skArc(sketch, "E108.0.6.1", {"start": v(30.76, 123.75) * mm, "mid": v(28.76, 125.75) * mm, "end": v(30.76, 127.75) * mm});
            skArc(sketch, "E108.0.6.2", {"start": v(45.76, 127.75) * mm, "mid": v(47.76, 125.75) * mm, "end": v(45.76, 123.75) * mm});
            skLineSegment(sketch, "E108.0.6.3", {"start": v(30.76, 127.75) * mm, "end": v(45.76, 127.75) * mm});
            skLineSegment(sketch, "E108.0.6.4", {"start": v(30.76, 123.75) * mm, "end": v(45.76, 123.75) * mm});
            skLineSegment(sketch, "E108.0.7.0", {"start": v(30.76, 133.75) * mm, "end": v(45.76, 133.75) * mm, "construction": true});
            skArc(sketch, "E108.0.7.1", {"start": v(30.76, 131.75) * mm, "mid": v(28.76, 133.75) * mm, "end": v(30.76, 135.75) * mm});
            skArc(sketch, "E108.0.7.2", {"start": v(45.76, 135.75) * mm, "mid": v(47.76, 133.75) * mm, "end": v(45.76, 131.75) * mm});
            skLineSegment(sketch, "E108.0.7.3", {"start": v(30.76, 135.75) * mm, "end": v(45.76, 135.75) * mm});
            skLineSegment(sketch, "E108.0.7.4", {"start": v(30.76, 131.75) * mm, "end": v(45.76, 131.75) * mm});
            skLineSegment(sketch, "E108.0.8.0", {"start": v(30.76, 141.75) * mm, "end": v(45.76, 141.75) * mm, "construction": true});
            skArc(sketch, "E108.0.8.1", {"start": v(30.76, 139.75) * mm, "mid": v(28.76, 141.75) * mm, "end": v(30.76, 143.75) * mm});
            skArc(sketch, "E108.0.8.2", {"start": v(45.76, 143.75) * mm, "mid": v(47.76, 141.75) * mm, "end": v(45.76, 139.75) * mm});
            skLineSegment(sketch, "E108.0.8.3", {"start": v(30.76, 143.75) * mm, "end": v(45.76, 143.75) * mm});
            skLineSegment(sketch, "E108.0.8.4", {"start": v(30.76, 139.75) * mm, "end": v(45.76, 139.75) * mm});
            skLineSegment(sketch, "E108.0.9.0", {"start": v(30.76, 149.75) * mm, "end": v(45.76, 149.75) * mm, "construction": true});
            skArc(sketch, "E108.0.9.1", {"start": v(30.76, 147.75) * mm, "mid": v(28.76, 149.75) * mm, "end": v(30.76, 151.75) * mm});
            skArc(sketch, "E108.0.9.2", {"start": v(45.76, 151.75) * mm, "mid": v(47.76, 149.75) * mm, "end": v(45.76, 147.75) * mm});
            skLineSegment(sketch, "E108.0.9.3", {"start": v(30.76, 151.75) * mm, "end": v(45.76, 151.75) * mm});
            skLineSegment(sketch, "E108.0.9.4", {"start": v(30.76, 147.75) * mm, "end": v(45.76, 147.75) * mm});
            skLineSegment(sketch, "E108.0.10.0", {"start": v(30.76, 157.75) * mm, "end": v(45.76, 157.75) * mm, "construction": true});
            skArc(sketch, "E108.0.10.1", {"start": v(30.76, 155.75) * mm, "mid": v(28.76, 157.75) * mm, "end": v(30.76, 159.75) * mm});
            skArc(sketch, "E108.0.10.2", {"start": v(45.76, 159.75) * mm, "mid": v(47.76, 157.75) * mm, "end": v(45.76, 155.75) * mm});
            skLineSegment(sketch, "E108.0.10.3", {"start": v(30.76, 159.75) * mm, "end": v(45.76, 159.75) * mm});
            skLineSegment(sketch, "E108.0.10.4", {"start": v(30.76, 155.75) * mm, "end": v(45.76, 155.75) * mm});
            skLineSegment(sketch, "E108.0.11.0", {"start": v(30.76, 165.75) * mm, "end": v(45.76, 165.75) * mm, "construction": true});
            skArc(sketch, "E108.0.11.1", {"start": v(30.76, 163.75) * mm, "mid": v(28.76, 165.75) * mm, "end": v(30.76, 167.75) * mm});
            skArc(sketch, "E108.0.11.2", {"start": v(45.76, 167.75) * mm, "mid": v(47.76, 165.75) * mm, "end": v(45.76, 163.75) * mm});
            skLineSegment(sketch, "E108.0.11.3", {"start": v(30.76, 167.75) * mm, "end": v(45.76, 167.75) * mm});
            skLineSegment(sketch, "E108.0.11.4", {"start": v(30.76, 163.75) * mm, "end": v(45.76, 163.75) * mm});
            skLineSegment(sketch, "E108.0.12.0", {"start": v(30.76, 173.75) * mm, "end": v(45.76, 173.75) * mm, "construction": true});
            skArc(sketch, "E108.0.12.1", {"start": v(30.76, 171.75) * mm, "mid": v(28.76, 173.75) * mm, "end": v(30.76, 175.75) * mm});
            skArc(sketch, "E108.0.12.2", {"start": v(45.76, 175.75) * mm, "mid": v(47.76, 173.75) * mm, "end": v(45.76, 171.75) * mm});
            skLineSegment(sketch, "E108.0.12.3", {"start": v(30.76, 175.75) * mm, "end": v(45.76, 175.75) * mm});
            skLineSegment(sketch, "E108.0.12.4", {"start": v(30.76, 171.75) * mm, "end": v(45.76, 171.75) * mm});
            skLineSegment(sketch, "E108.0.13.0", {"start": v(30.76, 181.75) * mm, "end": v(45.76, 181.75) * mm, "construction": true});
            skArc(sketch, "E108.0.13.1", {"start": v(30.76, 179.75) * mm, "mid": v(28.76, 181.75) * mm, "end": v(30.76, 183.75) * mm});
            skArc(sketch, "E108.0.13.2", {"start": v(45.76, 183.75) * mm, "mid": v(47.76, 181.75) * mm, "end": v(45.76, 179.75) * mm});
            skLineSegment(sketch, "E108.0.13.3", {"start": v(30.76, 183.75) * mm, "end": v(45.76, 183.75) * mm});
            skLineSegment(sketch, "E108.0.13.4", {"start": v(30.76, 179.75) * mm, "end": v(45.76, 179.75) * mm});
            skLineSegment(sketch, "E108.0.14.0", {"start": v(30.76, 189.75) * mm, "end": v(45.76, 189.75) * mm, "construction": true});
            skArc(sketch, "E108.0.14.1", {"start": v(30.76, 187.75) * mm, "mid": v(28.76, 189.75) * mm, "end": v(30.76, 191.75) * mm});
            skArc(sketch, "E108.0.14.2", {"start": v(45.76, 191.75) * mm, "mid": v(47.76, 189.75) * mm, "end": v(45.76, 187.75) * mm});
            skLineSegment(sketch, "E108.0.14.3", {"start": v(30.76, 191.75) * mm, "end": v(45.76, 191.75) * mm});
            skLineSegment(sketch, "E108.0.14.4", {"start": v(30.76, 187.75) * mm, "end": v(45.76, 187.75) * mm});
            skLineSegment(sketch, "E108.direction1", {"start": v(30.76, 75.75) * mm, "end": v(55.76, 75.75) * mm, "construction": true});
            skLineSegment(sketch, "E108.direction2", {"start": v(30.76, 75.75) * mm, "end": v(30.76, 83.75) * mm, "construction": true});
            skLineSegment(sketch, "E109.0.0.15", {"start": v(30.76, 197.75) * mm, "end": v(45.76, 197.75) * mm, "construction": true});
            skArc(sketch, "E109.3.0.15", {"start": v(30.76, 195.75) * mm, "mid": v(28.76, 197.75) * mm, "end": v(30.76, 199.75) * mm});
            skArc(sketch, "E109.7.0.15", {"start": v(45.76, 199.75) * mm, "mid": v(47.76, 197.75) * mm, "end": v(45.76, 195.75) * mm});
            skLineSegment(sketch, "E109.11.0.15", {"start": v(30.76, 199.75) * mm, "end": v(45.76, 199.75) * mm});
            skLineSegment(sketch, "E109.14.0.15", {"start": v(30.76, 195.75) * mm, "end": v(45.76, 195.75) * mm});
            skLineSegment(sketch, "E109.0.0.16", {"start": v(30.76, 205.75) * mm, "end": v(45.76, 205.75) * mm, "construction": true});
            skArc(sketch, "E109.3.0.16", {"start": v(30.76, 203.75) * mm, "mid": v(28.76, 205.75) * mm, "end": v(30.76, 207.75) * mm});
            skArc(sketch, "E109.7.0.16", {"start": v(45.76, 207.75) * mm, "mid": v(47.76, 205.75) * mm, "end": v(45.76, 203.75) * mm});
            skLineSegment(sketch, "E109.11.0.16", {"start": v(30.76, 207.75) * mm, "end": v(45.76, 207.75) * mm});
            skLineSegment(sketch, "E109.14.0.16", {"start": v(30.76, 203.75) * mm, "end": v(45.76, 203.75) * mm});
            skLineSegment(sketch, "E110.0.0.17", {"start": v(30.76, 213.75) * mm, "end": v(45.76, 213.75) * mm, "construction": true});
            skArc(sketch, "E110.3.0.17", {"start": v(30.76, 211.75) * mm, "mid": v(28.76, 213.75) * mm, "end": v(30.76, 215.75) * mm});
            skArc(sketch, "E110.7.0.17", {"start": v(45.76, 215.75) * mm, "mid": v(47.76, 213.75) * mm, "end": v(45.76, 211.75) * mm});
            skLineSegment(sketch, "E110.11.0.17", {"start": v(30.76, 215.75) * mm, "end": v(45.76, 215.75) * mm});
            skLineSegment(sketch, "E110.14.0.17", {"start": v(30.76, 211.75) * mm, "end": v(45.76, 211.75) * mm});
            skLineSegment(sketch, "E110.0.0.18", {"start": v(30.76, 221.75) * mm, "end": v(45.76, 221.75) * mm, "construction": true});
            skArc(sketch, "E110.3.0.18", {"start": v(30.76, 219.75) * mm, "mid": v(28.76, 221.75) * mm, "end": v(30.76, 223.75) * mm});
            skArc(sketch, "E110.7.0.18", {"start": v(45.76, 223.75) * mm, "mid": v(47.76, 221.75) * mm, "end": v(45.76, 219.75) * mm});
            skLineSegment(sketch, "E110.11.0.18", {"start": v(30.76, 223.75) * mm, "end": v(45.76, 223.75) * mm});
            skLineSegment(sketch, "E110.14.0.18", {"start": v(30.76, 219.75) * mm, "end": v(45.76, 219.75) * mm});
            skSolve(sketch);
        }
        {
            var Q0;
            Q0 = qSketchRegion(id + "F21", true);
            extrude(context, id + "F22", {"entities" : qUnion([Q0]), "operationType" : NewBodyOperationType.REMOVE, "oppositeDirection" : true, "depth" : 25 * mm});
        }
        {
            var Q0;
            Q0=qCreatedBy(makeId("Top.planeOp"),FACE);
            cPlane(context, id + "F23", {"entities" : qUnion([Q0]), "cplaneType" : CPlaneType.OFFSET, "offset" : 153 * mm, "oppositeDirection" : true, "width" : 150 * mm, "height" : 150 * mm});
        }
        {
            var Q0;
            Q0=qCreatedBy(id+"F23.planeOp",FACE);
            var sketch = newSketch(context, id + "F24", { "sketchPlane" : qUnion([Q0])});
            skLineSegment(sketch, "E111.bottom", {"start": v(-65.56, 22.42) * mm, "end": v(72.44, 22.42) * mm});
            skLineSegment(sketch, "E111.top", {"start": v(-65.56, 109.42) * mm, "end": v(72.44, 109.42) * mm});
            skLineSegment(sketch, "E111.left", {"start": v(-65.56, 22.42) * mm, "end": v(-65.56, 109.42) * mm});
            skLineSegment(sketch, "E111.right", {"start": v(72.44, 22.42) * mm, "end": v(72.44, 109.42) * mm});
            skLineSegment(sketch, "E112", {"start": v(3.44, 22.42) * mm, "end": v(3.44, 27.42) * mm, "construction": true});
            skLineSegment(sketch, "E113", {"start": v(3.44, 27.42) * mm, "end": v(13.44, 27.42) * mm});
            skLineSegment(sketch, "E114", {"start": v(13.44, 27.42) * mm, "end": v(18.44, 22.42) * mm});
            skLineSegment(sketch, "E115", {"start": v(3.44, 27.42) * mm, "end": v(-6.56, 27.42) * mm});
            skLineSegment(sketch, "E116", {"start": v(-6.56, 27.42) * mm, "end": v(-11.56, 22.42) * mm});
            skSolve(sketch);
        }
        {
            var Q0;
            {var subQ1=sQuery(id+"F24.wireOp",EDGE,"E111.top");Q0=makeQuery(id+"F24.imprint","IMPRINT",FACE,{"disambiguationData":[TD([[makeQuery(id+"F24.imprint","IMPRINT",EDGE,{"derivedFrom":subQ1}),-1.0]])]});}
            extrude(context, id + "F25", {"entities" : qUnion([Q0]), "depth" : 3 * mm});
        }
        {
            var Q0;
            Q0=makeQuery(id+"F25.opExtrude","SWEPT_BODY",BODY,{"disambiguationData":[OSD([sQuery(id+"F24.wireOp",EDGE,"E111.bottom"),sQuery(id+"F24.wireOp",EDGE,"E111.top"),sQuery(id+"F24.wireOp",EDGE,"E111.left"),sQuery(id+"F24.wireOp",EDGE,"E111.right"),sQuery(id+"F24.wireOp",EDGE,"ijy9X7zk-xbec-bhKK-NvL2-62svXoWdeAxU"),sQuery(id+"F24.wireOp",EDGE,"dnEH7a7q-0e2G-ZF1u-gQp3-ZGx2YlrUhsfq"),sQuery(id+"F24.wireOp",EDGE,"EYcrjZ5U-B8Tu-Hvld-BROV-cSRqyUUC4nfP"),sQuery(id+"F24.wireOp",EDGE,"lcQWckg9-mZXk-lsL4-PW7S-RH1iYC4EfrxX"),sQuery(id+"F24.wireOp",EDGE,"m4YSihPu-nfU7-MdAm-Gg2Q-VAeN7eaJ9XWN"),sQuery(id+"F24.wireOp",EDGE,"Pqck9NCv-W0KR-IoVA-u59r-mS94P2QdRFWv")])]});
            var Q1;
            Q1=makeQuery(id+"F25.opExtrude","SWEPT_FACE",FACE,{"disambiguationData":[OSD([sQuery(id+"F24.wireOp",EDGE,"E111.top")])]});
            mirror(context, id + "F26", {"operationType" : NewBodyOperationType.ADD, "entities" : qUnion([Q0]), "mirrorPlane" : qUnion([Q1])});
        }
        {
            var Q0;
            Q0=qCreatedBy(makeId("Front.planeOp"),FACE);
            cPlane(context, id + "F27", {"entities" : qUnion([Q0]), "cplaneType" : CPlaneType.OFFSET, "offset" : 376 * mm, "oppositeDirection" : true, "width" : 150 * mm, "height" : 150 * mm});
        }
        {
            var Q0;
            {var subQ0=makeQuery(id+"F25.opExtrude","CAP_FACE",FACE,{"disambiguationData":[OSD([sQuery(id+"F24.wireOp",EDGE,"E111.bottom"),sQuery(id+"F24.wireOp",EDGE,"E111.top"),sQuery(id+"F24.wireOp",EDGE,"E111.left"),sQuery(id+"F24.wireOp",EDGE,"E111.right"),sQuery(id+"F24.wireOp",EDGE,"ijy9X7zk-xbec-bhKK-NvL2-62svXoWdeAxU"),sQuery(id+"F24.wireOp",EDGE,"dnEH7a7q-0e2G-ZF1u-gQp3-ZGx2YlrUhsfq"),sQuery(id+"F24.wireOp",EDGE,"EYcrjZ5U-B8Tu-Hvld-BROV-cSRqyUUC4nfP"),sQuery(id+"F24.wireOp",EDGE,"lcQWckg9-mZXk-lsL4-PW7S-RH1iYC4EfrxX"),sQuery(id+"F24.wireOp",EDGE,"m4YSihPu-nfU7-MdAm-Gg2Q-VAeN7eaJ9XWN"),sQuery(id+"F24.wireOp",EDGE,"Pqck9NCv-W0KR-IoVA-u59r-mS94P2QdRFWv")])],"isStart":true});Q0=makeQuery(id+"F26.boolean.opBoolean","MERGE",FACE,{"derivedFrom":[subQ0,makeQuery(id+"F26.opPattern","COPY",FACE,{"derivedFrom":subQ0,"instanceName":"1"})]});}
            var sketch = newSketch(context, id + "F28", { "sketchPlane" : qUnion([Q0])});
            skLineSegment(sketch, "E117", {"start": v(-42.06, -172.42) * mm, "end": v(-42.06, -150.42) * mm, "construction": true});
            skLineSegment(sketch, "E118", {"start": v(-42.06, -150.42) * mm, "end": v(-42.06, -137.76) * mm, "construction": true});
            skLineSegment(sketch, "E119", {"start": v(-42.06, -137.76) * mm, "end": v(-42.06, -115.76) * mm, "construction": true});
            skLineSegment(sketch, "E120", {"start": v(-42.06, -115.76) * mm, "end": v(-42.06, -103.1) * mm, "construction": true});
            skLineSegment(sketch, "E121", {"start": v(-42.06, -103.1) * mm, "end": v(-42.06, -81.1) * mm, "construction": true});
            skLineSegment(sketch, "E122", {"start": v(-42.06, -81.1) * mm, "end": v(-42.06, -68.42) * mm, "construction": true});
            skLineSegment(sketch, "E123", {"start": v(-42.06, -172.42) * mm, "end": v(-42.06, -196.42) * mm, "construction": true});
            skLineSegment(sketch, "E124", {"start": v(-42.06, -68.42) * mm, "end": v(-42.06, -46.42) * mm, "construction": true});
            skLineSegment(sketch, "E125", {"start": v(-42.06, -46.42) * mm, "end": v(-42.06, -22.42) * mm, "construction": true});
            skArc(sketch, "E126.0.startCap", {"start": v(-37.06, -172.42) * mm, "mid": v(-42.06, -177.42) * mm, "end": v(-47.06, -172.42) * mm});
            skArc(sketch, "E126.0.endCap", {"start": v(-47.06, -150.42) * mm, "mid": v(-42.06, -145.42) * mm, "end": v(-37.06, -150.42) * mm});
            skLineSegment(sketch, "E126.0.left", {"start": v(-47.06, -172.42) * mm, "end": v(-47.06, -150.42) * mm});
            skLineSegment(sketch, "E126.0.right", {"start": v(-37.06, -172.42) * mm, "end": v(-37.06, -150.42) * mm});
            skArc(sketch, "E126.1.startCap", {"start": v(-37.06, -137.76) * mm, "mid": v(-42.06, -142.76) * mm, "end": v(-47.06, -137.76) * mm});
            skArc(sketch, "E126.1.endCap", {"start": v(-47.06, -115.76) * mm, "mid": v(-42.06, -110.76) * mm, "end": v(-37.06, -115.76) * mm});
            skLineSegment(sketch, "E126.1.left", {"start": v(-47.06, -137.76) * mm, "end": v(-47.06, -115.76) * mm});
            skLineSegment(sketch, "E126.1.right", {"start": v(-37.06, -137.76) * mm, "end": v(-37.06, -115.76) * mm});
            skArc(sketch, "E126.2.startCap", {"start": v(-37.06, -103.1) * mm, "mid": v(-42.06, -108.1) * mm, "end": v(-47.06, -103.1) * mm});
            skArc(sketch, "E126.2.endCap", {"start": v(-47.06, -81.1) * mm, "mid": v(-42.06, -76.1) * mm, "end": v(-37.06, -81.1) * mm});
            skLineSegment(sketch, "E126.2.left", {"start": v(-47.06, -103.1) * mm, "end": v(-47.06, -81.1) * mm});
            skLineSegment(sketch, "E126.2.right", {"start": v(-37.06, -103.1) * mm, "end": v(-37.06, -81.1) * mm});
            skArc(sketch, "E126.3.startCap", {"start": v(-37.06, -68.42) * mm, "mid": v(-42.06, -73.42) * mm, "end": v(-47.06, -68.42) * mm});
            skArc(sketch, "E126.3.endCap", {"start": v(-47.06, -46.42) * mm, "mid": v(-42.06, -41.42) * mm, "end": v(-37.06, -46.42) * mm});
            skLineSegment(sketch, "E126.3.left", {"start": v(-47.06, -68.42) * mm, "end": v(-47.06, -46.42) * mm});
            skLineSegment(sketch, "E126.3.right", {"start": v(-37.06, -68.42) * mm, "end": v(-37.06, -46.42) * mm});
            skArc(sketch, "E127.1.0.0", {"start": v(-19.06, -172.42) * mm, "mid": v(-24.06, -177.42) * mm, "end": v(-29.06, -172.42) * mm});
            skLineSegment(sketch, "E127.1.0.1", {"start": v(-19.06, -172.42) * mm, "end": v(-19.06, -150.42) * mm});
            skLineSegment(sketch, "E127.1.0.2", {"start": v(-29.06, -172.42) * mm, "end": v(-29.06, -150.42) * mm});
            skArc(sketch, "E127.1.0.3", {"start": v(-29.06, -150.42) * mm, "mid": v(-24.06, -145.42) * mm, "end": v(-19.06, -150.42) * mm});
            skArc(sketch, "E127.1.0.4", {"start": v(-19.06, -137.76) * mm, "mid": v(-24.06, -142.76) * mm, "end": v(-29.06, -137.76) * mm});
            skLineSegment(sketch, "E127.1.0.5", {"start": v(-19.06, -137.76) * mm, "end": v(-19.06, -115.76) * mm});
            skLineSegment(sketch, "E127.1.0.6", {"start": v(-29.06, -137.76) * mm, "end": v(-29.06, -115.76) * mm});
            skArc(sketch, "E127.1.0.7", {"start": v(-29.06, -115.76) * mm, "mid": v(-24.06, -110.76) * mm, "end": v(-19.06, -115.76) * mm});
            skLineSegment(sketch, "E127.1.0.8", {"start": v(-19.06, -103.1) * mm, "end": v(-19.06, -81.1) * mm});
            skArc(sketch, "E127.1.0.9", {"start": v(-19.06, -103.1) * mm, "mid": v(-24.06, -108.1) * mm, "end": v(-29.06, -103.1) * mm});
            skLineSegment(sketch, "E127.1.0.10", {"start": v(-29.06, -103.1) * mm, "end": v(-29.06, -81.1) * mm});
            skArc(sketch, "E127.1.0.11", {"start": v(-29.06, -81.1) * mm, "mid": v(-24.06, -76.1) * mm, "end": v(-19.06, -81.1) * mm});
            skArc(sketch, "E127.1.0.12", {"start": v(-19.06, -68.42) * mm, "mid": v(-24.06, -73.42) * mm, "end": v(-29.06, -68.42) * mm});
            skLineSegment(sketch, "E127.1.0.13", {"start": v(-19.06, -68.42) * mm, "end": v(-19.06, -46.42) * mm});
            skLineSegment(sketch, "E127.1.0.14", {"start": v(-29.06, -68.42) * mm, "end": v(-29.06, -46.42) * mm});
            skArc(sketch, "E127.1.0.15", {"start": v(-29.06, -46.42) * mm, "mid": v(-24.06, -41.42) * mm, "end": v(-19.06, -46.42) * mm});
            skArc(sketch, "E127.2.0.0", {"start": v(-1.06, -172.42) * mm, "mid": v(-6.06, -177.42) * mm, "end": v(-11.06, -172.42) * mm});
            skLineSegment(sketch, "E127.2.0.1", {"start": v(-1.06, -172.42) * mm, "end": v(-1.06, -150.42) * mm});
            skLineSegment(sketch, "E127.2.0.2", {"start": v(-11.06, -172.42) * mm, "end": v(-11.06, -150.42) * mm});
            skArc(sketch, "E127.2.0.3", {"start": v(-11.06, -150.42) * mm, "mid": v(-6.06, -145.42) * mm, "end": v(-1.06, -150.42) * mm});
            skArc(sketch, "E127.2.0.4", {"start": v(-1.06, -137.76) * mm, "mid": v(-6.06, -142.76) * mm, "end": v(-11.06, -137.76) * mm});
            skLineSegment(sketch, "E127.2.0.5", {"start": v(-1.06, -137.76) * mm, "end": v(-1.06, -115.76) * mm});
            skLineSegment(sketch, "E127.2.0.6", {"start": v(-11.06, -137.76) * mm, "end": v(-11.06, -115.76) * mm});
            skArc(sketch, "E127.2.0.7", {"start": v(-11.06, -115.76) * mm, "mid": v(-6.06, -110.76) * mm, "end": v(-1.06, -115.76) * mm});
            skLineSegment(sketch, "E127.2.0.8", {"start": v(-1.06, -103.1) * mm, "end": v(-1.06, -81.1) * mm});
            skArc(sketch, "E127.2.0.9", {"start": v(-1.06, -103.1) * mm, "mid": v(-6.06, -108.1) * mm, "end": v(-11.06, -103.1) * mm});
            skLineSegment(sketch, "E127.2.0.10", {"start": v(-11.06, -103.1) * mm, "end": v(-11.06, -81.1) * mm});
            skArc(sketch, "E127.2.0.11", {"start": v(-11.06, -81.1) * mm, "mid": v(-6.06, -76.1) * mm, "end": v(-1.06, -81.1) * mm});
            skArc(sketch, "E127.2.0.12", {"start": v(-1.06, -68.42) * mm, "mid": v(-6.06, -73.42) * mm, "end": v(-11.06, -68.42) * mm});
            skLineSegment(sketch, "E127.2.0.13", {"start": v(-1.06, -68.42) * mm, "end": v(-1.06, -46.42) * mm});
            skLineSegment(sketch, "E127.2.0.14", {"start": v(-11.06, -68.42) * mm, "end": v(-11.06, -46.42) * mm});
            skArc(sketch, "E127.2.0.15", {"start": v(-11.06, -46.42) * mm, "mid": v(-6.06, -41.42) * mm, "end": v(-1.06, -46.42) * mm});
            skArc(sketch, "E127.3.0.0", {"start": v(16.94, -172.42) * mm, "mid": v(11.94, -177.42) * mm, "end": v(6.94, -172.42) * mm});
            skLineSegment(sketch, "E127.3.0.1", {"start": v(16.94, -172.42) * mm, "end": v(16.94, -150.42) * mm});
            skLineSegment(sketch, "E127.3.0.2", {"start": v(6.94, -172.42) * mm, "end": v(6.94, -150.42) * mm});
            skArc(sketch, "E127.3.0.3", {"start": v(6.94, -150.42) * mm, "mid": v(11.94, -145.42) * mm, "end": v(16.94, -150.42) * mm});
            skArc(sketch, "E127.3.0.4", {"start": v(16.94, -137.76) * mm, "mid": v(11.94, -142.76) * mm, "end": v(6.94, -137.76) * mm});
            skLineSegment(sketch, "E127.3.0.5", {"start": v(16.94, -137.76) * mm, "end": v(16.94, -115.76) * mm});
            skLineSegment(sketch, "E127.3.0.6", {"start": v(6.94, -137.76) * mm, "end": v(6.94, -115.76) * mm});
            skArc(sketch, "E127.3.0.7", {"start": v(6.94, -115.76) * mm, "mid": v(11.94, -110.76) * mm, "end": v(16.94, -115.76) * mm});
            skLineSegment(sketch, "E127.3.0.8", {"start": v(16.94, -103.1) * mm, "end": v(16.94, -81.1) * mm});
            skArc(sketch, "E127.3.0.9", {"start": v(16.94, -103.1) * mm, "mid": v(11.94, -108.1) * mm, "end": v(6.94, -103.1) * mm});
            skLineSegment(sketch, "E127.3.0.10", {"start": v(6.94, -103.1) * mm, "end": v(6.94, -81.1) * mm});
            skArc(sketch, "E127.3.0.11", {"start": v(6.94, -81.1) * mm, "mid": v(11.94, -76.1) * mm, "end": v(16.94, -81.1) * mm});
            skArc(sketch, "E127.3.0.12", {"start": v(16.94, -68.42) * mm, "mid": v(11.94, -73.42) * mm, "end": v(6.94, -68.42) * mm});
            skLineSegment(sketch, "E127.3.0.13", {"start": v(16.94, -68.42) * mm, "end": v(16.94, -46.42) * mm});
            skLineSegment(sketch, "E127.3.0.14", {"start": v(6.94, -68.42) * mm, "end": v(6.94, -46.42) * mm});
            skArc(sketch, "E127.3.0.15", {"start": v(6.94, -46.42) * mm, "mid": v(11.94, -41.42) * mm, "end": v(16.94, -46.42) * mm});
            skArc(sketch, "E127.4.0.0", {"start": v(34.94, -172.42) * mm, "mid": v(29.94, -177.42) * mm, "end": v(24.94, -172.42) * mm});
            skLineSegment(sketch, "E127.4.0.1", {"start": v(34.94, -172.42) * mm, "end": v(34.94, -150.42) * mm});
            skLineSegment(sketch, "E127.4.0.2", {"start": v(24.94, -172.42) * mm, "end": v(24.94, -150.42) * mm});
            skArc(sketch, "E127.4.0.3", {"start": v(24.94, -150.42) * mm, "mid": v(29.94, -145.42) * mm, "end": v(34.94, -150.42) * mm});
            skArc(sketch, "E127.4.0.4", {"start": v(34.94, -137.76) * mm, "mid": v(29.94, -142.76) * mm, "end": v(24.94, -137.76) * mm});
            skLineSegment(sketch, "E127.4.0.5", {"start": v(34.94, -137.76) * mm, "end": v(34.94, -115.76) * mm});
            skLineSegment(sketch, "E127.4.0.6", {"start": v(24.94, -137.76) * mm, "end": v(24.94, -115.76) * mm});
            skArc(sketch, "E127.4.0.7", {"start": v(24.94, -115.76) * mm, "mid": v(29.94, -110.76) * mm, "end": v(34.94, -115.76) * mm});
            skLineSegment(sketch, "E127.4.0.8", {"start": v(34.94, -103.1) * mm, "end": v(34.94, -81.1) * mm});
            skArc(sketch, "E127.4.0.9", {"start": v(34.94, -103.1) * mm, "mid": v(29.94, -108.1) * mm, "end": v(24.94, -103.1) * mm});
            skLineSegment(sketch, "E127.4.0.10", {"start": v(24.94, -103.1) * mm, "end": v(24.94, -81.1) * mm});
            skArc(sketch, "E127.4.0.11", {"start": v(24.94, -81.1) * mm, "mid": v(29.94, -76.1) * mm, "end": v(34.94, -81.1) * mm});
            skArc(sketch, "E127.4.0.12", {"start": v(34.94, -68.42) * mm, "mid": v(29.94, -73.42) * mm, "end": v(24.94, -68.42) * mm});
            skLineSegment(sketch, "E127.4.0.13", {"start": v(34.94, -68.42) * mm, "end": v(34.94, -46.42) * mm});
            skLineSegment(sketch, "E127.4.0.14", {"start": v(24.94, -68.42) * mm, "end": v(24.94, -46.42) * mm});
            skArc(sketch, "E127.4.0.15", {"start": v(24.94, -46.42) * mm, "mid": v(29.94, -41.42) * mm, "end": v(34.94, -46.42) * mm});
            skArc(sketch, "E127.5.0.0", {"start": v(52.94, -172.42) * mm, "mid": v(47.94, -177.42) * mm, "end": v(42.94, -172.42) * mm});
            skLineSegment(sketch, "E127.5.0.1", {"start": v(52.94, -172.42) * mm, "end": v(52.94, -150.42) * mm});
            skLineSegment(sketch, "E127.5.0.2", {"start": v(42.94, -172.42) * mm, "end": v(42.94, -150.42) * mm});
            skArc(sketch, "E127.5.0.3", {"start": v(42.94, -150.42) * mm, "mid": v(47.94, -145.42) * mm, "end": v(52.94, -150.42) * mm});
            skArc(sketch, "E127.5.0.4", {"start": v(52.94, -137.76) * mm, "mid": v(47.94, -142.76) * mm, "end": v(42.94, -137.76) * mm});
            skLineSegment(sketch, "E127.5.0.5", {"start": v(52.94, -137.76) * mm, "end": v(52.94, -115.76) * mm});
            skLineSegment(sketch, "E127.5.0.6", {"start": v(42.94, -137.76) * mm, "end": v(42.94, -115.76) * mm});
            skArc(sketch, "E127.5.0.7", {"start": v(42.94, -115.76) * mm, "mid": v(47.94, -110.76) * mm, "end": v(52.94, -115.76) * mm});
            skLineSegment(sketch, "E127.5.0.8", {"start": v(52.94, -103.1) * mm, "end": v(52.94, -81.1) * mm});
            skArc(sketch, "E127.5.0.9", {"start": v(52.94, -103.1) * mm, "mid": v(47.94, -108.1) * mm, "end": v(42.94, -103.1) * mm});
            skLineSegment(sketch, "E127.5.0.10", {"start": v(42.94, -103.1) * mm, "end": v(42.94, -81.1) * mm});
            skArc(sketch, "E127.5.0.11", {"start": v(42.94, -81.1) * mm, "mid": v(47.94, -76.1) * mm, "end": v(52.94, -81.1) * mm});
            skArc(sketch, "E127.5.0.12", {"start": v(52.94, -68.42) * mm, "mid": v(47.94, -73.42) * mm, "end": v(42.94, -68.42) * mm});
            skLineSegment(sketch, "E127.5.0.13", {"start": v(52.94, -68.42) * mm, "end": v(52.94, -46.42) * mm});
            skLineSegment(sketch, "E127.5.0.14", {"start": v(42.94, -68.42) * mm, "end": v(42.94, -46.42) * mm});
            skArc(sketch, "E127.5.0.15", {"start": v(42.94, -46.42) * mm, "mid": v(47.94, -41.42) * mm, "end": v(52.94, -46.42) * mm});
            skLineSegment(sketch, "E127.direction1", {"start": v(-47.06, -172.42) * mm, "end": v(-29.06, -172.42) * mm, "construction": true});
            skSolve(sketch);
        }
        {
            var Q0;
            Q0=qSketchRegion(id+"F28",true);
            extrude(context, id + "F29", {"entities" : qUnion([Q0]), "operationType" : NewBodyOperationType.REMOVE, "oppositeDirection" : true, "depth" : 25 * mm});
        }
        {
            var Q0;
            Q0=qCreatedBy(id+"F27.planeOp",FACE);
            var sketch = newSketch(context, id + "F30", { "sketchPlane" : qUnion([Q0])});
            skLineSegment(sketch, "E128.bottom", {"start": v(-70, 118) * mm, "end": v(68, 118) * mm});
            skLineSegment(sketch, "E128.top", {"start": v(-70, 9.5) * mm, "end": v(68, 9.5) * mm});
            skLineSegment(sketch, "E128.left", {"start": v(-70, 118) * mm, "end": v(-70, 9.5) * mm});
            skLineSegment(sketch, "E128.right", {"start": v(68, 118) * mm, "end": v(68, 9.5) * mm});
            skLineSegment(sketch, "E129", {"start": v(68, 118) * mm, "end": v(68, 106.95) * mm});
            skLineSegment(sketch, "E130", {"start": v(68, 106.95) * mm, "end": v(64.95, 106.95) * mm});
            skLineSegment(sketch, "E131", {"start": v(64.95, 106.95) * mm, "end": v(64.95, 118) * mm});
            skLineSegment(sketch, "E132", {"start": v(-66.95, 118) * mm, "end": v(-66.95, 106.95) * mm});
            skLineSegment(sketch, "E133", {"start": v(-66.95, 106.95) * mm, "end": v(-70, 106.95) * mm});
            skSolve(sketch);
        }
        {
            var Q0;
            {var subQ1=sQuery(id+"F30.wireOp",EDGE,"E128.top");Q0=makeQuery(id+"F30.imprint","IMPRINT",FACE,{"disambiguationData":[TD([[makeQuery(id+"F30.imprint","IMPRINT",EDGE,{"derivedFrom":subQ1}),1.0]])]});}
            extrude(context, id + "F31", {"entities" : qUnion([Q0]), "depth" : 3 * mm});
        }
        {
            var Q0;
            Q0=makeQuery(id+"F31.opExtrude","SWEPT_BODY",BODY,{"disambiguationData":[OSD([sQuery(id+"F30.wireOp",EDGE,"E128.bottom"),sQuery(id+"F30.wireOp",EDGE,"E128.top"),sQuery(id+"F30.wireOp",EDGE,"E128.left"),sQuery(id+"F30.wireOp",EDGE,"E128.right"),sQuery(id+"F30.wireOp",EDGE,"88c43418-5c0f-4f09-8127-112137b7eb87"),sQuery(id+"F30.wireOp",EDGE,"1dde41ba-0d21-4c08-9e43-a64729d44614"),sQuery(id+"F30.wireOp",EDGE,"ccf2e9e3-9b64-4f2a-9f18-310bc790516a"),sQuery(id+"F30.wireOp",EDGE,"c5f426b9-73f2-4868-9408-4cfd947a191f"),sQuery(id+"F30.wireOp",EDGE,"cd8d91dd-9a42-4ae4-8430-5a7eccad3886"),sQuery(id+"F30.wireOp",EDGE,"f1dcae7c-8bd8-43e5-b7b1-ff3532f110ef")])]});
            var Q1;
            Q1=makeQuery(id+"F31.opExtrude","SWEPT_FACE",FACE,{"disambiguationData":[OSD([sQuery(id+"F30.wireOp",EDGE,"E128.top")])]});
            mirror(context, id + "F32", {"operationType" : NewBodyOperationType.ADD, "entities" : qUnion([Q0]), "mirrorPlane" : qUnion([Q1])});
        }
        {
            var Q0;
            {var subQ0=makeQuery(id+"F31.opExtrude","CAP_FACE",FACE,{"disambiguationData":[OSD([sQuery(id+"F30.wireOp",EDGE,"E128.bottom"),sQuery(id+"F30.wireOp",EDGE,"E128.top"),sQuery(id+"F30.wireOp",EDGE,"E128.left"),sQuery(id+"F30.wireOp",EDGE,"E128.right"),sQuery(id+"F30.wireOp",EDGE,"88c43418-5c0f-4f09-8127-112137b7eb87"),sQuery(id+"F30.wireOp",EDGE,"1dde41ba-0d21-4c08-9e43-a64729d44614"),sQuery(id+"F30.wireOp",EDGE,"ccf2e9e3-9b64-4f2a-9f18-310bc790516a"),sQuery(id+"F30.wireOp",EDGE,"c5f426b9-73f2-4868-9408-4cfd947a191f"),sQuery(id+"F30.wireOp",EDGE,"cd8d91dd-9a42-4ae4-8430-5a7eccad3886"),sQuery(id+"F30.wireOp",EDGE,"f1dcae7c-8bd8-43e5-b7b1-ff3532f110ef")])],"isStart":true});Q0=makeQuery(id+"F32.boolean.opBoolean","MERGE",FACE,{"derivedFrom":[subQ0,makeQuery(id+"F32.opPattern","COPY",FACE,{"derivedFrom":subQ0,"instanceName":"1"})]});}
            var sketch = newSketch(context, id + "F33", { "sketchPlane" : qUnion([Q0])});
            skLineSegment(sketch, "E134", {"start": v(-58, 106) * mm, "end": v(-58, -64) * mm, "construction": true});
            skLineSegment(sketch, "E135", {"start": v(-58, -64) * mm, "end": v(-68, -64) * mm, "construction": true});
            skLineSegment(sketch, "E136", {"start": v(-58, -62.7) * mm, "end": v(-49.9, -62.7) * mm, "construction": true});
            skLineSegment(sketch, "E137.bottom", {"start": v(-49.9, -70.65) * mm, "end": v(47.1, -70.65) * mm});
            skLineSegment(sketch, "E137.top", {"start": v(-49.9, -54.75) * mm, "end": v(47.1, -54.75) * mm});
            skLineSegment(sketch, "E137.left", {"start": v(-49.9, -70.65) * mm, "end": v(-49.9, -54.75) * mm});
            skLineSegment(sketch, "E137.right", {"start": v(47.1, -70.65) * mm, "end": v(47.1, -54.75) * mm});
            skLineSegment(sketch, "E138.bottom", {"start": v(-49.9, -75.05) * mm, "end": v(47.1, -75.05) * mm});
            skLineSegment(sketch, "E138.top", {"start": v(-49.9, -90.95) * mm, "end": v(47.1, -90.95) * mm});
            skLineSegment(sketch, "E138.left", {"start": v(-49.9, -75.05) * mm, "end": v(-49.9, -90.95) * mm});
            skLineSegment(sketch, "E138.right", {"start": v(47.1, -75.05) * mm, "end": v(47.1, -90.95) * mm});
            skLineSegment(sketch, "E139", {"start": v(47.1, -75.05) * mm, "end": v(47.1, -70.65) * mm, "construction": true});
            skLineSegment(sketch, "E140", {"start": v(47.1, -90.95) * mm, "end": v(47.1, -91.95) * mm, "construction": true});
            skLineSegment(sketch, "E141", {"start": v(47.1, -91.95) * mm, "end": v(-49.9, -91.95) * mm, "construction": true});
            skLineSegment(sketch, "E142", {"start": v(-49.9, -91.95) * mm, "end": v(-49.9, -90.95) * mm, "construction": true});
            skLineSegment(sketch, "E143", {"start": v(-58, -50.32) * mm, "end": v(51, -50.32) * mm, "construction": true});
            skLineSegment(sketch, "E144.left", {"start": v(51, -50.32) * mm, "end": v(51, -90.95) * mm});
            skLineSegment(sketch, "E145", {"start": v(47.1, -54.75) * mm, "end": v(51, -54.75) * mm, "construction": true});
            skLineSegment(sketch, "E146", {"start": v(47.1, -90.95) * mm, "end": v(51, -90.95) * mm, "construction": true});
            skLineSegment(sketch, "E147.bottom", {"start": v(-15.6, 109.5) * mm, "end": v(-60.3, 109.5) * mm});
            skLineSegment(sketch, "E148", {"start": v(-60.3, 109.5) * mm, "end": v(-60.3, -50.4) * mm});
            skLineSegment(sketch, "E149", {"start": v(-60.3, -50.4) * mm, "end": v(-15.6, -50.4) * mm});
            skLineSegment(sketch, "E150", {"start": v(-15.6, -50.4) * mm, "end": v(-15.6, 109.5) * mm});
            skArc(sketch, "E151", {"start": v(-59.55, 109.5) * mm, "mid": v(-60.83, 110.03) * mm, "end": v(-60.3, 108.75) * mm});
            skArc(sketch, "E152", {"start": v(-15.6, 108.75) * mm, "mid": v(-15.07, 110.03) * mm, "end": v(-16.35, 109.5) * mm});
            skArc(sketch, "E153", {"start": v(-16.35, -50.32) * mm, "mid": v(-15.1, -50.96) * mm, "end": v(-15.6, -49.65) * mm});
            skArc(sketch, "E154", {"start": v(-60.3, -49.65) * mm, "mid": v(-60.83, -50.93) * mm, "end": v(-59.55, -50.4) * mm});
            skLineSegment(sketch, "E155", {"start": v(51, -90.95) * mm, "end": v(54, -90.95) * mm});
            skLineSegment(sketch, "E156", {"start": v(54, -90.95) * mm, "end": v(74, -90.95) * mm, "construction": true});
            skLineSegment(sketch, "E157", {"start": v(74, -50.32) * mm, "end": v(74, -78.95) * mm});
            skLineSegment(sketch, "E158", {"start": v(74, -78.95) * mm, "end": v(74, -90.95) * mm});
            skLineSegment(sketch, "E159", {"start": v(54, -90.95) * mm, "end": v(57, -87.95) * mm});
            skLineSegment(sketch, "E160", {"start": v(57, -87.95) * mm, "end": v(66.95, -87.95) * mm});
            skLineSegment(sketch, "E161", {"start": v(66.95, -87.95) * mm, "end": v(70, -87.95) * mm});
            skLineSegment(sketch, "E162", {"start": v(51, -50.32) * mm, "end": v(64, -37.32) * mm});
            skLineSegment(sketch, "E163", {"start": v(64, -37.32) * mm, "end": v(70, -37.32) * mm});
            skLineSegment(sketch, "E164", {"start": v(70, -37.32) * mm, "end": v(70, -87.95) * mm});
            skSolve(sketch);
        }
        {
            var Q0;
            {var subQ0=makeQuery(id+"F31.opExtrude","CAP_FACE",FACE,{"disambiguationData":[OSD([sQuery(id+"F30.wireOp",EDGE,"E128.bottom"),sQuery(id+"F30.wireOp",EDGE,"E128.top"),sQuery(id+"F30.wireOp",EDGE,"E128.left"),sQuery(id+"F30.wireOp",EDGE,"E128.right"),sQuery(id+"F30.wireOp",EDGE,"88c43418-5c0f-4f09-8127-112137b7eb87"),sQuery(id+"F30.wireOp",EDGE,"1dde41ba-0d21-4c08-9e43-a64729d44614"),sQuery(id+"F30.wireOp",EDGE,"ccf2e9e3-9b64-4f2a-9f18-310bc790516a"),sQuery(id+"F30.wireOp",EDGE,"c5f426b9-73f2-4868-9408-4cfd947a191f"),sQuery(id+"F30.wireOp",EDGE,"cd8d91dd-9a42-4ae4-8430-5a7eccad3886"),sQuery(id+"F30.wireOp",EDGE,"f1dcae7c-8bd8-43e5-b7b1-ff3532f110ef")])],"isStart":true});Q0=makeQuery(id+"F32.boolean.opBoolean","MERGE",FACE,{"derivedFrom":[subQ0,makeQuery(id+"F32.opPattern","COPY",FACE,{"derivedFrom":subQ0,"instanceName":"1"})]});}
            var sketch = newSketch(context, id + "F34", { "sketchPlane" : qUnion([Q0])});
            skLineSegment(sketch, "E165", {"start": v(-1, 118) * mm, "end": v(-1, 78) * mm, "construction": true});
            skLineSegment(sketch, "E166", {"start": v(-1, 78) * mm, "end": v(-1, 54) * mm, "construction": true});
            skLineSegment(sketch, "E167", {"start": v(-1, 54) * mm, "end": v(-1, 40) * mm, "construction": true});
            skLineSegment(sketch, "E168", {"start": v(-1, 40) * mm, "end": v(-1, 16) * mm, "construction": true});
            skLineSegment(sketch, "E169", {"start": v(-1, 16) * mm, "end": v(-1, 2) * mm, "construction": true});
            skLineSegment(sketch, "E170", {"start": v(-1, 2) * mm, "end": v(-1, -22) * mm, "construction": true});
            skArc(sketch, "E171.0.startCap", {"start": v(-4, 78) * mm, "mid": v(-1, 81) * mm, "end": v(2, 78) * mm});
            skArc(sketch, "E171.0.endCap", {"start": v(2, 54) * mm, "mid": v(-1, 51) * mm, "end": v(-4, 54) * mm});
            skLineSegment(sketch, "E171.0.left", {"start": v(2, 78) * mm, "end": v(2, 54) * mm});
            skLineSegment(sketch, "E171.0.right", {"start": v(-4, 78) * mm, "end": v(-4, 54) * mm});
            skArc(sketch, "E172.0.startCap", {"start": v(-4, 40) * mm, "mid": v(-1, 43) * mm, "end": v(2, 40) * mm});
            skArc(sketch, "E172.0.endCap", {"start": v(2, 16) * mm, "mid": v(-1, 13) * mm, "end": v(-4, 16) * mm});
            skLineSegment(sketch, "E172.0.left", {"start": v(2, 40) * mm, "end": v(2, 16) * mm});
            skLineSegment(sketch, "E172.0.right", {"start": v(-4, 40) * mm, "end": v(-4, 16) * mm});
            skArc(sketch, "E172.1.startCap", {"start": v(-4, 2) * mm, "mid": v(-1, 5) * mm, "end": v(2, 2) * mm});
            skArc(sketch, "E172.1.endCap", {"start": v(2, -22) * mm, "mid": v(-1, -25) * mm, "end": v(-4, -22) * mm});
            skLineSegment(sketch, "E172.1.left", {"start": v(2, 2) * mm, "end": v(2, -22) * mm});
            skLineSegment(sketch, "E172.1.right", {"start": v(-4, 2) * mm, "end": v(-4, -22) * mm});
            skLineSegment(sketch, "E173.1.0.0", {"start": v(10, 2) * mm, "end": v(10, -22) * mm});
            skLineSegment(sketch, "E173.1.0.2", {"start": v(10, 78) * mm, "end": v(10, 54) * mm});
            skArc(sketch, "E173.1.0.3", {"start": v(10, 40) * mm, "mid": v(13, 43) * mm, "end": v(16, 40) * mm});
            skArc(sketch, "E173.1.0.5", {"start": v(10, 2) * mm, "mid": v(13, 5) * mm, "end": v(16, 2) * mm});
            skArc(sketch, "E173.1.0.7", {"start": v(16, -22) * mm, "mid": v(13, -25) * mm, "end": v(10, -22) * mm});
            skLineSegment(sketch, "E173.1.0.8", {"start": v(16, 78) * mm, "end": v(16, 54) * mm});
            skArc(sketch, "E173.1.0.9", {"start": v(16, 54) * mm, "mid": v(13, 51) * mm, "end": v(10, 54) * mm});
            skArc(sketch, "E173.1.0.10", {"start": v(10, 78) * mm, "mid": v(13, 81) * mm, "end": v(16, 78) * mm});
            skLineSegment(sketch, "E173.1.0.13", {"start": v(13, 2) * mm, "end": v(13, -22) * mm, "construction": true});
            skLineSegment(sketch, "E173.1.0.14", {"start": v(13, 16) * mm, "end": v(13, 2) * mm, "construction": true});
            skLineSegment(sketch, "E173.1.0.15", {"start": v(13, 40) * mm, "end": v(13, 16) * mm, "construction": true});
            skLineSegment(sketch, "E173.1.0.16", {"start": v(16, 2) * mm, "end": v(16, -22) * mm});
            skLineSegment(sketch, "E173.1.0.17", {"start": v(13, 54) * mm, "end": v(13, 40) * mm, "construction": true});
            skLineSegment(sketch, "E173.1.0.18", {"start": v(13, 78) * mm, "end": v(13, 54) * mm, "construction": true});
            skLineSegment(sketch, "E173.1.0.20", {"start": v(10, 40) * mm, "end": v(10, 16) * mm});
            skLineSegment(sketch, "E173.1.0.21", {"start": v(16, 40) * mm, "end": v(16, 16) * mm});
            skArc(sketch, "E173.1.0.22", {"start": v(16, 16) * mm, "mid": v(13, 13) * mm, "end": v(10, 16) * mm});
            skLineSegment(sketch, "E173.2.0.0", {"start": v(24, 2) * mm, "end": v(24, -22) * mm});
            skLineSegment(sketch, "E173.2.0.2", {"start": v(24, 78) * mm, "end": v(24, 54) * mm});
            skArc(sketch, "E173.2.0.3", {"start": v(24, 40) * mm, "mid": v(27, 43) * mm, "end": v(30, 40) * mm});
            skArc(sketch, "E173.2.0.5", {"start": v(24, 2) * mm, "mid": v(27, 5) * mm, "end": v(30, 2) * mm});
            skArc(sketch, "E173.2.0.7", {"start": v(30, -22) * mm, "mid": v(27, -25) * mm, "end": v(24, -22) * mm});
            skLineSegment(sketch, "E173.2.0.8", {"start": v(30, 78) * mm, "end": v(30, 54) * mm});
            skArc(sketch, "E173.2.0.9", {"start": v(30, 54) * mm, "mid": v(27, 51) * mm, "end": v(24, 54) * mm});
            skArc(sketch, "E173.2.0.10", {"start": v(24, 78) * mm, "mid": v(27, 81) * mm, "end": v(30, 78) * mm});
            skLineSegment(sketch, "E173.2.0.13", {"start": v(27, 2) * mm, "end": v(27, -22) * mm, "construction": true});
            skLineSegment(sketch, "E173.2.0.14", {"start": v(27, 16) * mm, "end": v(27, 2) * mm, "construction": true});
            skLineSegment(sketch, "E173.2.0.15", {"start": v(27, 40) * mm, "end": v(27, 16) * mm, "construction": true});
            skLineSegment(sketch, "E173.2.0.16", {"start": v(30, 2) * mm, "end": v(30, -22) * mm});
            skLineSegment(sketch, "E173.2.0.17", {"start": v(27, 54) * mm, "end": v(27, 40) * mm, "construction": true});
            skLineSegment(sketch, "E173.2.0.18", {"start": v(27, 78) * mm, "end": v(27, 54) * mm, "construction": true});
            skLineSegment(sketch, "E173.2.0.20", {"start": v(24, 40) * mm, "end": v(24, 16) * mm});
            skLineSegment(sketch, "E173.2.0.21", {"start": v(30, 40) * mm, "end": v(30, 16) * mm});
            skArc(sketch, "E173.2.0.22", {"start": v(30, 16) * mm, "mid": v(27, 13) * mm, "end": v(24, 16) * mm});
            skLineSegment(sketch, "E174.0.3.0", {"start": v(38, 2) * mm, "end": v(38, -22) * mm});
            skLineSegment(sketch, "E174.7.3.0", {"start": v(38, 78) * mm, "end": v(38, 54) * mm});
            skArc(sketch, "E174.10.3.0", {"start": v(38, 40) * mm, "mid": v(41, 43) * mm, "end": v(44, 40) * mm});
            skArc(sketch, "E174.17.3.0", {"start": v(38, 2) * mm, "mid": v(41, 5) * mm, "end": v(44, 2) * mm});
            skArc(sketch, "E174.25.3.0", {"start": v(44, -22) * mm, "mid": v(41, -25) * mm, "end": v(38, -22) * mm});
            skLineSegment(sketch, "E174.29.3.0", {"start": v(44, 78) * mm, "end": v(44, 54) * mm});
            skArc(sketch, "E174.32.3.0", {"start": v(44, 54) * mm, "mid": v(41, 51) * mm, "end": v(38, 54) * mm});
            skArc(sketch, "E174.36.3.0", {"start": v(38, 78) * mm, "mid": v(41, 81) * mm, "end": v(44, 78) * mm});
            skLineSegment(sketch, "E174.46.3.0", {"start": v(41, 2) * mm, "end": v(41, -22) * mm, "construction": true});
            skLineSegment(sketch, "E174.49.3.0", {"start": v(41, 16) * mm, "end": v(41, 2) * mm, "construction": true});
            skLineSegment(sketch, "E174.52.3.0", {"start": v(41, 40) * mm, "end": v(41, 16) * mm, "construction": true});
            skLineSegment(sketch, "E174.55.3.0", {"start": v(44, 2) * mm, "end": v(44, -22) * mm});
            skLineSegment(sketch, "E174.58.3.0", {"start": v(41, 54) * mm, "end": v(41, 40) * mm, "construction": true});
            skLineSegment(sketch, "E174.61.3.0", {"start": v(41, 78) * mm, "end": v(41, 54) * mm, "construction": true});
            skLineSegment(sketch, "E174.67.3.0", {"start": v(38, 40) * mm, "end": v(38, 16) * mm});
            skLineSegment(sketch, "E174.70.3.0", {"start": v(44, 40) * mm, "end": v(44, 16) * mm});
            skArc(sketch, "E174.73.3.0", {"start": v(44, 16) * mm, "mid": v(41, 13) * mm, "end": v(38, 16) * mm});
            skLineSegment(sketch, "E175", {"start": v(13, 78) * mm, "end": v(-1, 78) * mm, "construction": true});
            skLineSegment(sketch, "E176", {"start": v(27, 78) * mm, "end": v(13, 78) * mm, "construction": true});
            skLineSegment(sketch, "E177", {"start": v(41, 78) * mm, "end": v(27, 78) * mm, "construction": true});
            skLineSegment(sketch, "E178", {"start": v(6.25, 110) * mm, "end": v(33.75, 110) * mm});
            skLineSegment(sketch, "E179", {"start": v(6.25, 110) * mm, "end": v(6.25, 97) * mm});
            skLineSegment(sketch, "E180", {"start": v(6.25, 97) * mm, "end": v(6.25, 90.2) * mm, "construction": true});
            skLineSegment(sketch, "E181", {"start": v(6.25, 90.2) * mm, "end": v(12, 90.2) * mm, "construction": true});
            skLineSegment(sketch, "E182", {"start": v(12, 90.2) * mm, "end": v(28, 90.2) * mm});
            skLineSegment(sketch, "E183", {"start": v(28, 90.2) * mm, "end": v(33.75, 90.2) * mm, "construction": true});
            skLineSegment(sketch, "E184", {"start": v(33.75, 90.2) * mm, "end": v(33.75, 97) * mm, "construction": true});
            skLineSegment(sketch, "E185", {"start": v(33.75, 97) * mm, "end": v(33.75, 110) * mm});
            skLineSegment(sketch, "E186", {"start": v(6.25, 97) * mm, "end": v(12, 90.2) * mm});
            skLineSegment(sketch, "E187", {"start": v(28, 90.2) * mm, "end": v(33.75, 97) * mm});
            skLineSegment(sketch, "E188", {"start": v(20, 90.2) * mm, "end": v(20, 110) * mm, "construction": true});
            skLineSegment(sketch, "E189", {"start": v(33.75, 100.6) * mm, "end": v(39.95, 100.6) * mm, "construction": true});
            skLineSegment(sketch, "E190", {"start": v(6.25, 101) * mm, "end": v(0.05, 101) * mm, "construction": true});
            skCircle(sketch, "E191", {"center": v(39.95, 100.6) * mm, "radius": 1.5 * mm});
            skCircle(sketch, "E192", {"center": v(0.05, 101) * mm, "radius": 1.5 * mm});
            skLineSegment(sketch, "E193", {"start": v(20, 110) * mm, "end": v(20, 118) * mm, "construction": true});
            skLineSegment(sketch, "E194", {"start": v(20, 90.2) * mm, "end": v(20, 78) * mm, "construction": true});
            skSolve(sketch);
        }
        {
            var Q0;
            Q0=qSketchRegion(id+"F33",true);
            var Q1;
            Q1=qSketchRegion(id+"F34",true);
            extrude(context, id + "F35", {"entities" : qUnion([Q0, Q1]), "operationType" : NewBodyOperationType.REMOVE, "oppositeDirection" : true, "depth" : 25 * mm});
        }
        {
            var Q0;
            Q0=makeQuery(id+"F35.boolean.opBoolean","COPY",EDGE,{"derivedFrom":makeQuery(id+"F35.opExtrude","SWEPT_EDGE",EDGE,{"disambiguationData":[OSD([sQuery(id+"F33.wireOp",EDGE,"E137.top"),sQuery(id+"F33.wireOp",EDGE,"E137.left")])]})});
            var Q1;
            Q1=makeQuery(id+"F35.boolean.opBoolean","COPY",EDGE,{"derivedFrom":makeQuery(id+"F35.opExtrude","SWEPT_EDGE",EDGE,{"disambiguationData":[OSD([sQuery(id+"F33.wireOp",EDGE,"E137.bottom"),sQuery(id+"F33.wireOp",EDGE,"E137.left")])]})});
            var Q2;
            Q2=makeQuery(id+"F35.boolean.opBoolean","COPY",EDGE,{"derivedFrom":makeQuery(id+"F35.opExtrude","SWEPT_EDGE",EDGE,{"disambiguationData":[OSD([sQuery(id+"F33.wireOp",EDGE,"E138.bottom"),sQuery(id+"F33.wireOp",EDGE,"E138.left")])]})});
            var Q3;
            Q3=makeQuery(id+"F35.boolean.opBoolean","COPY",EDGE,{"derivedFrom":makeQuery(id+"F35.opExtrude","SWEPT_EDGE",EDGE,{"disambiguationData":[OSD([sQuery(id+"F33.wireOp",EDGE,"E138.top"),sQuery(id+"F33.wireOp",EDGE,"E138.left")])]})});
            var Q4;
            Q4=makeQuery(id+"F35.boolean.opBoolean","COPY",EDGE,{"derivedFrom":makeQuery(id+"F35.opExtrude","SWEPT_EDGE",EDGE,{"disambiguationData":[OSD([sQuery(id+"F33.wireOp",EDGE,"E138.top"),sQuery(id+"F33.wireOp",EDGE,"E138.right")])]})});
            var Q5;
            Q5=makeQuery(id+"F35.boolean.opBoolean","COPY",EDGE,{"derivedFrom":makeQuery(id+"F35.opExtrude","SWEPT_EDGE",EDGE,{"disambiguationData":[OSD([sQuery(id+"F33.wireOp",EDGE,"E138.bottom"),sQuery(id+"F33.wireOp",EDGE,"E138.right")])]})});
            var Q6;
            Q6=makeQuery(id+"F35.boolean.opBoolean","COPY",EDGE,{"derivedFrom":makeQuery(id+"F35.opExtrude","SWEPT_EDGE",EDGE,{"disambiguationData":[OSD([sQuery(id+"F33.wireOp",EDGE,"E137.bottom"),sQuery(id+"F33.wireOp",EDGE,"E137.right")])]})});
            chamfer(context, id + "F36", {"entities" : qUnion([Q0, Q1, Q2, Q3, Q4, Q5, Q6]), "width" : 2 * mm, "tangentPropagation" : true});
        }
    });
